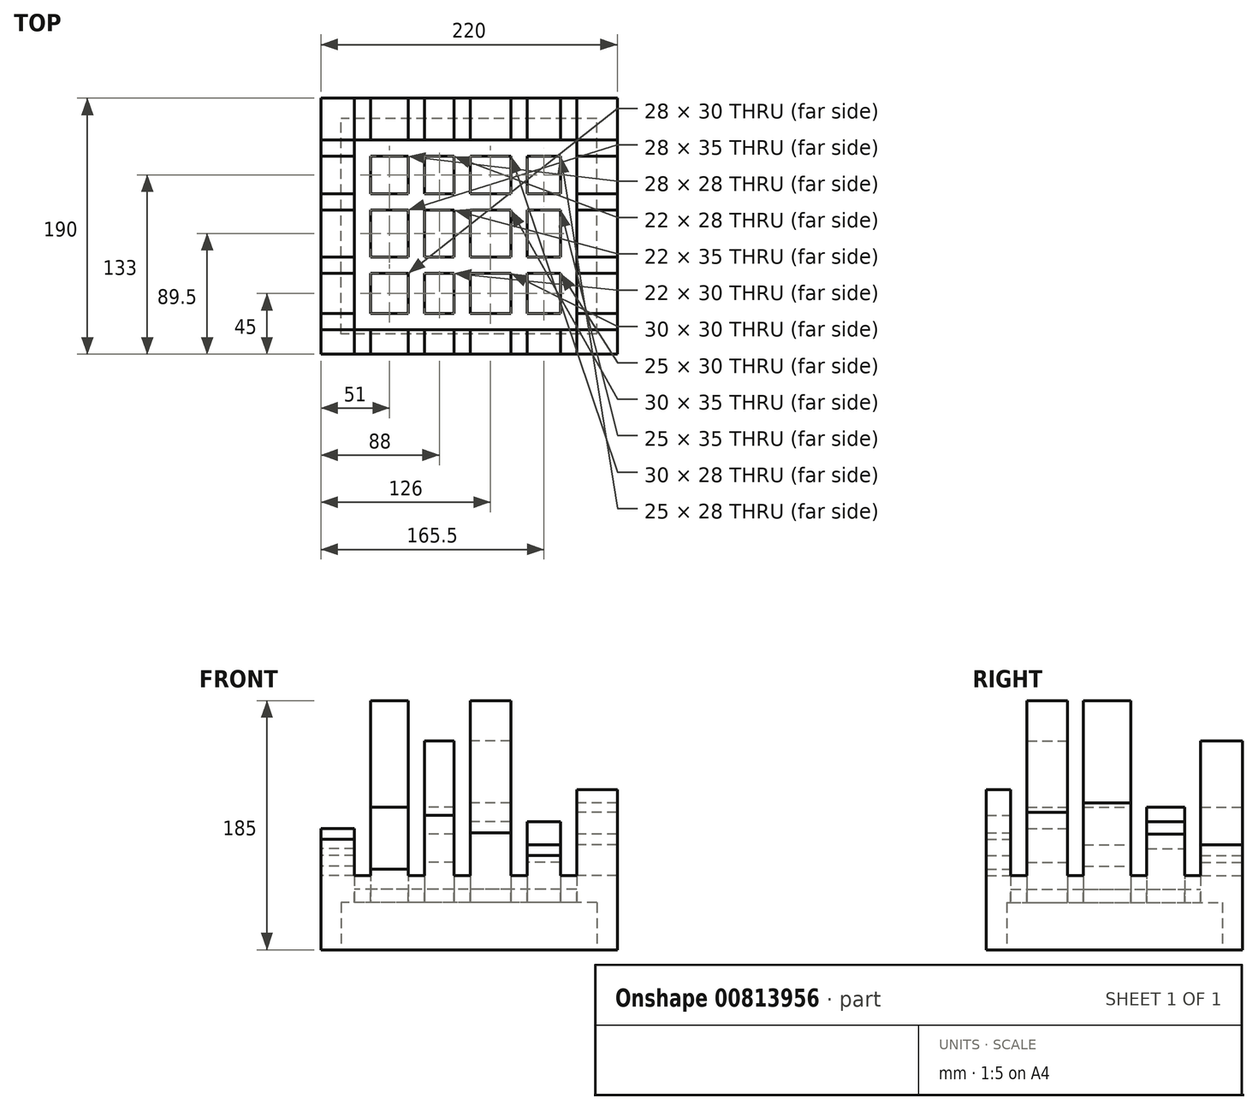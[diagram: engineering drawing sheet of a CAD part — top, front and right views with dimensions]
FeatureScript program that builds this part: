
annotation { "Feature Type Name" : "Feature", "Feature Type Description" : "" }
export const myFeature = defineFeature(function(context is Context, id is Id, definition is map)
    precondition{}
    {
        {
            var Q0;
            Q0=qCreatedBy(makeId("Top.planeOp"),FACE);
            var sketch = newSketch(context, id + "F0", { "sketchPlane" : qUnion([Q0])});
            skLineSegment(sketch, "E0.bottom", {"start": v(110, -95) * mm, "end": v(-110, -95) * mm});
            skLineSegment(sketch, "E0.top", {"start": v(110, 95) * mm, "end": v(-110, 95) * mm});
            skLineSegment(sketch, "E0.left", {"start": v(110, -95) * mm, "end": v(110, 95) * mm});
            skLineSegment(sketch, "E0.right", {"start": v(-110, -95) * mm, "end": v(-110, 95) * mm});
            skPoint(sketch, "E0.middle", {"position": v(0, 0) * mm});
            skLineSegment(sketch, "E1.0", {"start": v(-85, -95) * mm, "end": v(-85, 95) * mm});
            skLineSegment(sketch, "E2.0", {"start": v(-73, -95) * mm, "end": v(-73, 95) * mm});
            skLineSegment(sketch, "E3.0", {"start": v(-45, -95) * mm, "end": v(-45, 95) * mm});
            skLineSegment(sketch, "E4.0", {"start": v(-33, -95) * mm, "end": v(-33, 95) * mm});
            skLineSegment(sketch, "E5.0", {"start": v(-11, -95) * mm, "end": v(-11, 95) * mm});
            skLineSegment(sketch, "E6.0", {"start": v(1, -95) * mm, "end": v(1, 95) * mm});
            skLineSegment(sketch, "E7.0", {"start": v(31, -95) * mm, "end": v(31, 95) * mm});
            skLineSegment(sketch, "E8.0", {"start": v(43, -95) * mm, "end": v(43, 95) * mm});
            skLineSegment(sketch, "E9.0", {"start": v(68, -95) * mm, "end": v(68, 95) * mm});
            skLineSegment(sketch, "E10.0", {"start": v(80, -95) * mm, "end": v(80, 95) * mm});
            skLineSegment(sketch, "E11.0", {"start": v(110, -77) * mm, "end": v(-110, -77) * mm});
            skLineSegment(sketch, "E12.0", {"start": v(110, -65) * mm, "end": v(-110, -65) * mm});
            skLineSegment(sketch, "E13.0", {"start": v(110, -35) * mm, "end": v(-110, -35) * mm});
            skLineSegment(sketch, "E14.0", {"start": v(110, -23) * mm, "end": v(-110, -23) * mm});
            skLineSegment(sketch, "E15.0", {"start": v(110, 12) * mm, "end": v(-110, 12) * mm});
            skLineSegment(sketch, "E16.0", {"start": v(110, 24) * mm, "end": v(-110, 24) * mm});
            skLineSegment(sketch, "E17.0", {"start": v(110, 52) * mm, "end": v(-110, 52) * mm});
            skLineSegment(sketch, "E18.0", {"start": v(110, 64) * mm, "end": v(-110, 64) * mm});
            skSolve(sketch);
        }
        {
            var Q0;
            {var subQ0=sQuery(id+"F0.wireOp",EDGE,"E0.right");var subQ1=sQuery(id+"F0.wireOp",EDGE,"E0.top");var subQ2=makeQuery(id+"F0.imprint","INTERSECT",VERTEX,{"derivedFrom":[subQ1,subQ0]});Q0=makeQuery(id+"F0.imprint","IMPRINT",FACE,{"disambiguationData":[TD([[makeQuery(id+"F0.imprint","IMPRINT",EDGE,{"disambiguationData":[TD([[subQ2,1.0]])],"derivedFrom":subQ1}),1.0]])]});}
            extrude(context, id + "F1", {"entities" : qUnion([Q0]), "depth" : 25 * mm, "offsetDistance" : 25 * mm});
        }
        {
            var Q0;
            {var subQ0=sQuery(id+"F0.wireOp",EDGE,"E16.0");var subQ1=sQuery(id+"F0.wireOp",EDGE,"E0.right");var subQ2=makeQuery(id+"F0.imprint","INTERSECT",VERTEX,{"derivedFrom":[subQ1,subQ0]});Q0=makeQuery(id+"F0.imprint","IMPRINT",FACE,{"disambiguationData":[TD([[makeQuery(id+"F0.imprint","IMPRINT",EDGE,{"disambiguationData":[TD([[subQ2,-1.0]])],"derivedFrom":subQ1}),-1.0]])]});}
            extrude(context, id + "F2", {"entities" : qUnion([Q0]), "depth" : 30 * mm, "offsetDistance" : 25 * mm});
        }
        {
            var Q0;
            {var subQ0=sQuery(id+"F0.wireOp",EDGE,"E14.0");var subQ1=sQuery(id+"F0.wireOp",EDGE,"E0.right");var subQ2=makeQuery(id+"F0.imprint","INTERSECT",VERTEX,{"derivedFrom":[subQ1,subQ0]});Q0=makeQuery(id+"F0.imprint","IMPRINT",FACE,{"disambiguationData":[TD([[makeQuery(id+"F0.imprint","IMPRINT",EDGE,{"disambiguationData":[TD([[subQ2,-1.0]])],"derivedFrom":subQ1}),-1.0]])]});}
            extrude(context, id + "F3", {"entities" : qUnion([Q0]), "depth" : 17 * mm, "offsetDistance" : 25 * mm});
        }
        {
            var Q0;
            {var subQ0=sQuery(id+"F0.wireOp",EDGE,"E12.0");var subQ1=sQuery(id+"F0.wireOp",EDGE,"E0.right");var subQ2=makeQuery(id+"F0.imprint","INTERSECT",VERTEX,{"derivedFrom":[subQ1,subQ0]});Q0=makeQuery(id+"F0.imprint","IMPRINT",FACE,{"disambiguationData":[TD([[makeQuery(id+"F0.imprint","IMPRINT",EDGE,{"disambiguationData":[TD([[subQ2,-1.0]])],"derivedFrom":subQ1}),-1.0]])]});}
            extrude(context, id + "F4", {"entities" : qUnion([Q0]), "depth" : 45 * mm, "offsetDistance" : 25 * mm});
        }
        {
            var Q0;
            {var subQ0=sQuery(id+"F0.wireOp",EDGE,"E0.right");var subQ1=sQuery(id+"F0.wireOp",EDGE,"E0.bottom");var subQ2=makeQuery(id+"F0.imprint","INTERSECT",VERTEX,{"derivedFrom":[subQ1,subQ0]});Q0=makeQuery(id+"F0.imprint","IMPRINT",FACE,{"disambiguationData":[TD([[makeQuery(id+"F0.imprint","IMPRINT",EDGE,{"disambiguationData":[TD([[subQ2,1.0]])],"derivedFrom":subQ1}),-1.0]])]});}
            extrude(context, id + "F5", {"entities" : qUnion([Q0]), "depth" : 37 * mm, "offsetDistance" : 25 * mm});
        }
        {
            var Q0;
            {var subQ0=sQuery(id+"F0.wireOp",EDGE,"E2.0");var subQ1=sQuery(id+"F0.wireOp",EDGE,"E0.bottom");var subQ2=makeQuery(id+"F0.imprint","INTERSECT",VERTEX,{"derivedFrom":[subQ1,subQ0]});Q0=makeQuery(id+"F0.imprint","IMPRINT",FACE,{"disambiguationData":[TD([[makeQuery(id+"F0.imprint","IMPRINT",EDGE,{"disambiguationData":[TD([[subQ2,1.0]])],"derivedFrom":subQ1}),-1.0]])]});}
            extrude(context, id + "F6", {"entities" : qUnion([Q0]), "depth" : 15 * mm, "offsetDistance" : 25 * mm});
        }
        {
            var Q0;
            {var subQ0=sQuery(id+"F0.wireOp",EDGE,"E4.0");var subQ1=sQuery(id+"F0.wireOp",EDGE,"E0.bottom");var subQ2=makeQuery(id+"F0.imprint","INTERSECT",VERTEX,{"derivedFrom":[subQ1,subQ0]});Q0=makeQuery(id+"F0.imprint","IMPRINT",FACE,{"disambiguationData":[TD([[makeQuery(id+"F0.imprint","IMPRINT",EDGE,{"disambiguationData":[TD([[subQ2,1.0]])],"derivedFrom":subQ1}),-1.0]])]});}
            extrude(context, id + "F7", {"entities" : qUnion([Q0]), "depth" : 55 * mm, "offsetDistance" : 25 * mm});
        }
        {
            var Q0;
            {var subQ0=sQuery(id+"F0.wireOp",EDGE,"E6.0");var subQ1=sQuery(id+"F0.wireOp",EDGE,"E0.bottom");var subQ2=makeQuery(id+"F0.imprint","INTERSECT",VERTEX,{"derivedFrom":[subQ1,subQ0]});Q0=makeQuery(id+"F0.imprint","IMPRINT",FACE,{"disambiguationData":[TD([[makeQuery(id+"F0.imprint","IMPRINT",EDGE,{"disambiguationData":[TD([[subQ2,1.0]])],"derivedFrom":subQ1}),-1.0]])]});}
            extrude(context, id + "F8", {"entities" : qUnion([Q0]), "depth" : 42 * mm, "offsetDistance" : 25 * mm});
        }
        {
            var Q0;
            {var subQ0=sQuery(id+"F0.wireOp",EDGE,"E8.0");var subQ1=sQuery(id+"F0.wireOp",EDGE,"E0.bottom");var subQ2=makeQuery(id+"F0.imprint","INTERSECT",VERTEX,{"derivedFrom":[subQ1,subQ0]});Q0=makeQuery(id+"F0.imprint","IMPRINT",FACE,{"disambiguationData":[TD([[makeQuery(id+"F0.imprint","IMPRINT",EDGE,{"disambiguationData":[TD([[subQ2,1.0]])],"derivedFrom":subQ1}),-1.0]])]});}
            extrude(context, id + "F9", {"entities" : qUnion([Q0]), "depth" : 25 * mm, "offsetDistance" : 25 * mm});
        }
        {
            var Q0;
            {var subQ0=sQuery(id+"F0.wireOp",EDGE,"E0.left");var subQ1=sQuery(id+"F0.wireOp",EDGE,"E0.bottom");var subQ2=makeQuery(id+"F0.imprint","INTERSECT",VERTEX,{"derivedFrom":[subQ1,subQ0]});Q0=makeQuery(id+"F0.imprint","IMPRINT",FACE,{"disambiguationData":[TD([[makeQuery(id+"F0.imprint","IMPRINT",EDGE,{"disambiguationData":[TD([[subQ2,-1.0]])],"derivedFrom":subQ1}),-1.0]])]});}
            extrude(context, id + "F10", {"entities" : qUnion([Q0]), "depth" : 74 * mm, "offsetDistance" : 25 * mm});
        }
        {
            var Q0;
            {var subQ0=sQuery(id+"F0.wireOp",EDGE,"E12.0");var subQ1=sQuery(id+"F0.wireOp",EDGE,"E0.left");var subQ2=makeQuery(id+"F0.imprint","INTERSECT",VERTEX,{"derivedFrom":[subQ1,subQ0]});Q0=makeQuery(id+"F0.imprint","IMPRINT",FACE,{"disambiguationData":[TD([[makeQuery(id+"F0.imprint","IMPRINT",EDGE,{"disambiguationData":[TD([[subQ2,-1.0]])],"derivedFrom":subQ1}),1.0]])]});}
            extrude(context, id + "F11", {"entities" : qUnion([Q0]), "depth" : 57 * mm, "offsetDistance" : 25 * mm});
        }
        {
            var Q0;
            {var subQ0=sQuery(id+"F0.wireOp",EDGE,"E14.0");var subQ1=sQuery(id+"F0.wireOp",EDGE,"E0.left");var subQ2=makeQuery(id+"F0.imprint","INTERSECT",VERTEX,{"derivedFrom":[subQ1,subQ0]});Q0=makeQuery(id+"F0.imprint","IMPRINT",FACE,{"disambiguationData":[TD([[makeQuery(id+"F0.imprint","IMPRINT",EDGE,{"disambiguationData":[TD([[subQ2,-1.0]])],"derivedFrom":subQ1}),1.0]])]});}
            var Q1;
            {var subQ0=sQuery(id+"F0.wireOp",EDGE,"E14.0");var subQ1=sQuery(id+"F0.wireOp",EDGE,"E6.0");var subQ2=makeQuery(id+"F0.imprint","INTERSECT",VERTEX,{"derivedFrom":[subQ1,subQ0]});Q1=makeQuery(id+"F0.imprint","IMPRINT",FACE,{"disambiguationData":[TD([[makeQuery(id+"F0.imprint","IMPRINT",EDGE,{"disambiguationData":[TD([[subQ2,-1.0]])],"derivedFrom":subQ1}),-1.0]])]});}
            extrude(context, id + "F12", {"entities" : qUnion([Q0, Q1]), "depth" : 64 * mm, "offsetDistance" : 25 * mm});
        }
        {
            var Q0;
            {var subQ0=sQuery(id+"F0.wireOp",EDGE,"E16.0");var subQ1=sQuery(id+"F0.wireOp",EDGE,"E0.left");var subQ2=makeQuery(id+"F0.imprint","INTERSECT",VERTEX,{"derivedFrom":[subQ1,subQ0]});Q0=makeQuery(id+"F0.imprint","IMPRINT",FACE,{"disambiguationData":[TD([[makeQuery(id+"F0.imprint","IMPRINT",EDGE,{"disambiguationData":[TD([[subQ2,-1.0]])],"derivedFrom":subQ1}),1.0]])]});}
            var Q1;
            {var subQ0=sQuery(id+"F0.wireOp",EDGE,"E16.0");var subQ1=sQuery(id+"F0.wireOp",EDGE,"E4.0");var subQ2=makeQuery(id+"F0.imprint","INTERSECT",VERTEX,{"derivedFrom":[subQ1,subQ0]});Q1=makeQuery(id+"F0.imprint","IMPRINT",FACE,{"disambiguationData":[TD([[makeQuery(id+"F0.imprint","IMPRINT",EDGE,{"disambiguationData":[TD([[subQ2,-1.0]])],"derivedFrom":subQ1}),-1.0]])]});}
            extrude(context, id + "F13", {"entities" : qUnion([Q0, Q1]), "depth" : 41 * mm, "offsetDistance" : 25 * mm});
        }
        {
            var Q0;
            {var subQ0=sQuery(id+"F0.wireOp",EDGE,"E0.left");var subQ1=sQuery(id+"F0.wireOp",EDGE,"E0.top");var subQ2=makeQuery(id+"F0.imprint","INTERSECT",VERTEX,{"derivedFrom":[subQ1,subQ0]});Q0=makeQuery(id+"F0.imprint","IMPRINT",FACE,{"disambiguationData":[TD([[makeQuery(id+"F0.imprint","IMPRINT",EDGE,{"disambiguationData":[TD([[subQ2,-1.0]])],"derivedFrom":subQ1}),1.0]])]});}
            var Q1;
            {var subQ0=sQuery(id+"F0.wireOp",EDGE,"E14.0");var subQ1=sQuery(id+"F0.wireOp",EDGE,"E8.0");var subQ2=makeQuery(id+"F0.imprint","INTERSECT",VERTEX,{"derivedFrom":[subQ1,subQ0]});Q1=makeQuery(id+"F0.imprint","IMPRINT",FACE,{"disambiguationData":[TD([[makeQuery(id+"F0.imprint","IMPRINT",EDGE,{"disambiguationData":[TD([[subQ2,-1.0]])],"derivedFrom":subQ1}),-1.0]])]});}
            extrude(context, id + "F14", {"entities" : qUnion([Q0, Q1]), "depth" : 33 * mm, "offsetDistance" : 25 * mm});
        }
        {
            var Q0;
            {var subQ0=sQuery(id+"F0.wireOp",EDGE,"E6.0");var subQ1=sQuery(id+"F0.wireOp",EDGE,"E0.top");var subQ2=makeQuery(id+"F0.imprint","INTERSECT",VERTEX,{"derivedFrom":[subQ1,subQ0]});Q0=makeQuery(id+"F0.imprint","IMPRINT",FACE,{"disambiguationData":[TD([[makeQuery(id+"F0.imprint","IMPRINT",EDGE,{"disambiguationData":[TD([[subQ2,1.0]])],"derivedFrom":subQ1}),1.0]])]});}
            var Q1;
            {var subQ0=sQuery(id+"F0.wireOp",EDGE,"E12.0");var subQ1=sQuery(id+"F0.wireOp",EDGE,"E4.0");var subQ2=makeQuery(id+"F0.imprint","INTERSECT",VERTEX,{"derivedFrom":[subQ1,subQ0]});Q1=makeQuery(id+"F0.imprint","IMPRINT",FACE,{"disambiguationData":[TD([[makeQuery(id+"F0.imprint","IMPRINT",EDGE,{"disambiguationData":[TD([[subQ2,-1.0]])],"derivedFrom":subQ1}),-1.0]])]});}
            extrude(context, id + "F15", {"entities" : qUnion([Q0, Q1]), "depth" : 110 * mm, "offsetDistance" : 25 * mm});
        }
        {
            var Q0;
            {var subQ0=sQuery(id+"F0.wireOp",EDGE,"E14.0");var subQ1=sQuery(id+"F0.wireOp",EDGE,"E2.0");var subQ2=makeQuery(id+"F0.imprint","INTERSECT",VERTEX,{"derivedFrom":[subQ1,subQ0]});Q0=makeQuery(id+"F0.imprint","IMPRINT",FACE,{"disambiguationData":[TD([[makeQuery(id+"F0.imprint","IMPRINT",EDGE,{"disambiguationData":[TD([[subQ2,-1.0]])],"derivedFrom":subQ1}),-1.0]])]});}
            var Q1;
            {var subQ0=sQuery(id+"F0.wireOp",EDGE,"E12.0");var subQ1=sQuery(id+"F0.wireOp",EDGE,"E6.0");var subQ2=makeQuery(id+"F0.imprint","INTERSECT",VERTEX,{"derivedFrom":[subQ1,subQ0]});Q1=makeQuery(id+"F0.imprint","IMPRINT",FACE,{"disambiguationData":[TD([[makeQuery(id+"F0.imprint","IMPRINT",EDGE,{"disambiguationData":[TD([[subQ2,-1.0]])],"derivedFrom":subQ1}),-1.0]])]});}
            extrude(context, id + "F16", {"entities" : qUnion([Q0, Q1]), "depth" : 140 * mm, "offsetDistance" : 25 * mm});
        }
        {
            var Q0;
            {var subQ0=sQuery(id+"F0.wireOp",EDGE,"E16.0");var subQ1=sQuery(id+"F0.wireOp",EDGE,"E6.0");var subQ2=makeQuery(id+"F0.imprint","INTERSECT",VERTEX,{"derivedFrom":[subQ1,subQ0]});Q0=makeQuery(id+"F0.imprint","IMPRINT",FACE,{"disambiguationData":[TD([[makeQuery(id+"F0.imprint","IMPRINT",EDGE,{"disambiguationData":[TD([[subQ2,-1.0]])],"derivedFrom":subQ1}),-1.0]])]});}
            var Q1;
            {var subQ0=sQuery(id+"F0.wireOp",EDGE,"E16.0");var subQ1=sQuery(id+"F0.wireOp",EDGE,"E8.0");var subQ2=makeQuery(id+"F0.imprint","INTERSECT",VERTEX,{"derivedFrom":[subQ1,subQ0]});Q1=makeQuery(id+"F0.imprint","IMPRINT",FACE,{"disambiguationData":[TD([[makeQuery(id+"F0.imprint","IMPRINT",EDGE,{"disambiguationData":[TD([[subQ2,-1.0]])],"derivedFrom":subQ1}),-1.0]])]});}
            extrude(context, id + "F17", {"entities" : qUnion([Q0, Q1]), "depth" : 50 * mm, "offsetDistance" : 25 * mm});
        }
        {
            var Q0;
            {var subQ0=sQuery(id+"F0.wireOp",EDGE,"E2.0");var subQ1=sQuery(id+"F0.wireOp",EDGE,"E0.top");var subQ2=makeQuery(id+"F0.imprint","INTERSECT",VERTEX,{"derivedFrom":[subQ1,subQ0]});Q0=makeQuery(id+"F0.imprint","IMPRINT",FACE,{"disambiguationData":[TD([[makeQuery(id+"F0.imprint","IMPRINT",EDGE,{"disambiguationData":[TD([[subQ2,1.0]])],"derivedFrom":subQ1}),1.0]])]});}
            var Q1;
            {var subQ0=sQuery(id+"F0.wireOp",EDGE,"E16.0");var subQ1=sQuery(id+"F0.wireOp",EDGE,"E2.0");var subQ2=makeQuery(id+"F0.imprint","INTERSECT",VERTEX,{"derivedFrom":[subQ1,subQ0]});Q1=makeQuery(id+"F0.imprint","IMPRINT",FACE,{"disambiguationData":[TD([[makeQuery(id+"F0.imprint","IMPRINT",EDGE,{"disambiguationData":[TD([[subQ2,-1.0]])],"derivedFrom":subQ1}),-1.0]])]});}
            var Q2;
            {var subQ0=sQuery(id+"F0.wireOp",EDGE,"E14.0");var subQ1=sQuery(id+"F0.wireOp",EDGE,"E4.0");var subQ2=makeQuery(id+"F0.imprint","INTERSECT",VERTEX,{"derivedFrom":[subQ1,subQ0]});Q2=makeQuery(id+"F0.imprint","IMPRINT",FACE,{"disambiguationData":[TD([[makeQuery(id+"F0.imprint","IMPRINT",EDGE,{"disambiguationData":[TD([[subQ2,-1.0]])],"derivedFrom":subQ1}),-1.0]])]});}
            var Q3;
            {var subQ0=sQuery(id+"F0.wireOp",EDGE,"E12.0");var subQ1=sQuery(id+"F0.wireOp",EDGE,"E2.0");var subQ2=makeQuery(id+"F0.imprint","INTERSECT",VERTEX,{"derivedFrom":[subQ1,subQ0]});Q3=makeQuery(id+"F0.imprint","IMPRINT",FACE,{"disambiguationData":[TD([[makeQuery(id+"F0.imprint","IMPRINT",EDGE,{"disambiguationData":[TD([[subQ2,-1.0]])],"derivedFrom":subQ1}),-1.0]])]});}
            extrude(context, id + "F18", {"entities" : qUnion([Q0, Q1, Q2, Q3]), "depth" : 61 * mm, "offsetDistance" : 25 * mm});
        }
        {
            var Q0;
            {var subQ0=sQuery(id+"F0.wireOp",EDGE,"E4.0");var subQ1=sQuery(id+"F0.wireOp",EDGE,"E0.top");var subQ2=makeQuery(id+"F0.imprint","INTERSECT",VERTEX,{"derivedFrom":[subQ1,subQ0]});Q0=makeQuery(id+"F0.imprint","IMPRINT",FACE,{"disambiguationData":[TD([[makeQuery(id+"F0.imprint","IMPRINT",EDGE,{"disambiguationData":[TD([[subQ2,1.0]])],"derivedFrom":subQ1}),1.0]])]});}
            var Q1;
            {var subQ0=sQuery(id+"F0.wireOp",EDGE,"E8.0");var subQ1=sQuery(id+"F0.wireOp",EDGE,"E0.top");var subQ2=makeQuery(id+"F0.imprint","INTERSECT",VERTEX,{"derivedFrom":[subQ1,subQ0]});Q1=makeQuery(id+"F0.imprint","IMPRINT",FACE,{"disambiguationData":[TD([[makeQuery(id+"F0.imprint","IMPRINT",EDGE,{"disambiguationData":[TD([[subQ2,1.0]])],"derivedFrom":subQ1}),1.0]])]});}
            var Q2;
            {var subQ0=sQuery(id+"F0.wireOp",EDGE,"E12.0");var subQ1=sQuery(id+"F0.wireOp",EDGE,"E8.0");var subQ2=makeQuery(id+"F0.imprint","INTERSECT",VERTEX,{"derivedFrom":[subQ1,subQ0]});Q2=makeQuery(id+"F0.imprint","IMPRINT",FACE,{"disambiguationData":[TD([[makeQuery(id+"F0.imprint","IMPRINT",EDGE,{"disambiguationData":[TD([[subQ2,-1.0]])],"derivedFrom":subQ1}),-1.0]])]});}
            extrude(context, id + "F19", {"entities" : qUnion([Q0, Q1, Q2]), "depth" : 20 * mm, "offsetDistance" : 25 * mm});
        }
        {
            var Q0;
            {var subQ0=sQuery(id+"F0.wireOp",EDGE,"E17.0");var subQ1=sQuery(id+"F0.wireOp",EDGE,"E0.right");var subQ2=makeQuery(id+"F0.imprint","INTERSECT",VERTEX,{"derivedFrom":[subQ1,subQ0]});Q0=makeQuery(id+"F0.imprint","IMPRINT",FACE,{"disambiguationData":[TD([[makeQuery(id+"F0.imprint","IMPRINT",EDGE,{"disambiguationData":[TD([[subQ2,-1.0]])],"derivedFrom":subQ1}),-1.0]])]});}
            var Q1;
            {var subQ0=sQuery(id+"F0.wireOp",EDGE,"E15.0");var subQ1=sQuery(id+"F0.wireOp",EDGE,"E0.right");var subQ2=makeQuery(id+"F0.imprint","INTERSECT",VERTEX,{"derivedFrom":[subQ1,subQ0]});Q1=makeQuery(id+"F0.imprint","IMPRINT",FACE,{"disambiguationData":[TD([[makeQuery(id+"F0.imprint","IMPRINT",EDGE,{"disambiguationData":[TD([[subQ2,-1.0]])],"derivedFrom":subQ1}),-1.0]])]});}
            var Q2;
            {var subQ0=sQuery(id+"F0.wireOp",EDGE,"E13.0");var subQ1=sQuery(id+"F0.wireOp",EDGE,"E0.right");var subQ2=makeQuery(id+"F0.imprint","INTERSECT",VERTEX,{"derivedFrom":[subQ1,subQ0]});Q2=makeQuery(id+"F0.imprint","IMPRINT",FACE,{"disambiguationData":[TD([[makeQuery(id+"F0.imprint","IMPRINT",EDGE,{"disambiguationData":[TD([[subQ2,-1.0]])],"derivedFrom":subQ1}),-1.0]])]});}
            var Q3;
            {var subQ0=sQuery(id+"F0.wireOp",EDGE,"E11.0");var subQ1=sQuery(id+"F0.wireOp",EDGE,"E0.right");var subQ2=makeQuery(id+"F0.imprint","INTERSECT",VERTEX,{"derivedFrom":[subQ1,subQ0]});Q3=makeQuery(id+"F0.imprint","IMPRINT",FACE,{"disambiguationData":[TD([[makeQuery(id+"F0.imprint","IMPRINT",EDGE,{"disambiguationData":[TD([[subQ2,-1.0]])],"derivedFrom":subQ1}),-1.0]])]});}
            var Q4;
            {var subQ0=sQuery(id+"F0.wireOp",EDGE,"E1.0");var subQ1=sQuery(id+"F0.wireOp",EDGE,"E0.bottom");var subQ2=makeQuery(id+"F0.imprint","INTERSECT",VERTEX,{"derivedFrom":[subQ1,subQ0]});Q4=makeQuery(id+"F0.imprint","IMPRINT",FACE,{"disambiguationData":[TD([[makeQuery(id+"F0.imprint","IMPRINT",EDGE,{"disambiguationData":[TD([[subQ2,1.0]])],"derivedFrom":subQ1}),-1.0]])]});}
            var Q5;
            {var subQ0=sQuery(id+"F0.wireOp",EDGE,"E3.0");var subQ1=sQuery(id+"F0.wireOp",EDGE,"E0.bottom");var subQ2=makeQuery(id+"F0.imprint","INTERSECT",VERTEX,{"derivedFrom":[subQ1,subQ0]});Q5=makeQuery(id+"F0.imprint","IMPRINT",FACE,{"disambiguationData":[TD([[makeQuery(id+"F0.imprint","IMPRINT",EDGE,{"disambiguationData":[TD([[subQ2,1.0]])],"derivedFrom":subQ1}),-1.0]])]});}
            var Q6;
            {var subQ0=sQuery(id+"F0.wireOp",EDGE,"E5.0");var subQ1=sQuery(id+"F0.wireOp",EDGE,"E0.bottom");var subQ2=makeQuery(id+"F0.imprint","INTERSECT",VERTEX,{"derivedFrom":[subQ1,subQ0]});Q6=makeQuery(id+"F0.imprint","IMPRINT",FACE,{"disambiguationData":[TD([[makeQuery(id+"F0.imprint","IMPRINT",EDGE,{"disambiguationData":[TD([[subQ2,1.0]])],"derivedFrom":subQ1}),-1.0]])]});}
            var Q7;
            {var subQ0=sQuery(id+"F0.wireOp",EDGE,"E7.0");var subQ1=sQuery(id+"F0.wireOp",EDGE,"E0.bottom");var subQ2=makeQuery(id+"F0.imprint","INTERSECT",VERTEX,{"derivedFrom":[subQ1,subQ0]});Q7=makeQuery(id+"F0.imprint","IMPRINT",FACE,{"disambiguationData":[TD([[makeQuery(id+"F0.imprint","IMPRINT",EDGE,{"disambiguationData":[TD([[subQ2,1.0]])],"derivedFrom":subQ1}),-1.0]])]});}
            var Q8;
            {var subQ0=sQuery(id+"F0.wireOp",EDGE,"E9.0");var subQ1=sQuery(id+"F0.wireOp",EDGE,"E0.bottom");var subQ2=makeQuery(id+"F0.imprint","INTERSECT",VERTEX,{"derivedFrom":[subQ1,subQ0]});Q8=makeQuery(id+"F0.imprint","IMPRINT",FACE,{"disambiguationData":[TD([[makeQuery(id+"F0.imprint","IMPRINT",EDGE,{"disambiguationData":[TD([[subQ2,1.0]])],"derivedFrom":subQ1}),-1.0]])]});}
            var Q9;
            {var subQ0=sQuery(id+"F0.wireOp",EDGE,"E11.0");var subQ1=sQuery(id+"F0.wireOp",EDGE,"E0.left");var subQ2=makeQuery(id+"F0.imprint","INTERSECT",VERTEX,{"derivedFrom":[subQ1,subQ0]});Q9=makeQuery(id+"F0.imprint","IMPRINT",FACE,{"disambiguationData":[TD([[makeQuery(id+"F0.imprint","IMPRINT",EDGE,{"disambiguationData":[TD([[subQ2,-1.0]])],"derivedFrom":subQ1}),1.0]])]});}
            var Q10;
            {var subQ0=sQuery(id+"F0.wireOp",EDGE,"E13.0");var subQ1=sQuery(id+"F0.wireOp",EDGE,"E0.left");var subQ2=makeQuery(id+"F0.imprint","INTERSECT",VERTEX,{"derivedFrom":[subQ1,subQ0]});Q10=makeQuery(id+"F0.imprint","IMPRINT",FACE,{"disambiguationData":[TD([[makeQuery(id+"F0.imprint","IMPRINT",EDGE,{"disambiguationData":[TD([[subQ2,-1.0]])],"derivedFrom":subQ1}),1.0]])]});}
            var Q11;
            {var subQ0=sQuery(id+"F0.wireOp",EDGE,"E15.0");var subQ1=sQuery(id+"F0.wireOp",EDGE,"E0.left");var subQ2=makeQuery(id+"F0.imprint","INTERSECT",VERTEX,{"derivedFrom":[subQ1,subQ0]});Q11=makeQuery(id+"F0.imprint","IMPRINT",FACE,{"disambiguationData":[TD([[makeQuery(id+"F0.imprint","IMPRINT",EDGE,{"disambiguationData":[TD([[subQ2,-1.0]])],"derivedFrom":subQ1}),1.0]])]});}
            var Q12;
            {var subQ0=sQuery(id+"F0.wireOp",EDGE,"E17.0");var subQ1=sQuery(id+"F0.wireOp",EDGE,"E0.left");var subQ2=makeQuery(id+"F0.imprint","INTERSECT",VERTEX,{"derivedFrom":[subQ1,subQ0]});Q12=makeQuery(id+"F0.imprint","IMPRINT",FACE,{"disambiguationData":[TD([[makeQuery(id+"F0.imprint","IMPRINT",EDGE,{"disambiguationData":[TD([[subQ2,-1.0]])],"derivedFrom":subQ1}),1.0]])]});}
            var Q13;
            {var subQ0=sQuery(id+"F0.wireOp",EDGE,"E9.0");var subQ1=sQuery(id+"F0.wireOp",EDGE,"E0.top");var subQ2=makeQuery(id+"F0.imprint","INTERSECT",VERTEX,{"derivedFrom":[subQ1,subQ0]});Q13=makeQuery(id+"F0.imprint","IMPRINT",FACE,{"disambiguationData":[TD([[makeQuery(id+"F0.imprint","IMPRINT",EDGE,{"disambiguationData":[TD([[subQ2,1.0]])],"derivedFrom":subQ1}),1.0]])]});}
            var Q14;
            {var subQ0=sQuery(id+"F0.wireOp",EDGE,"E7.0");var subQ1=sQuery(id+"F0.wireOp",EDGE,"E0.top");var subQ2=makeQuery(id+"F0.imprint","INTERSECT",VERTEX,{"derivedFrom":[subQ1,subQ0]});Q14=makeQuery(id+"F0.imprint","IMPRINT",FACE,{"disambiguationData":[TD([[makeQuery(id+"F0.imprint","IMPRINT",EDGE,{"disambiguationData":[TD([[subQ2,1.0]])],"derivedFrom":subQ1}),1.0]])]});}
            var Q15;
            {var subQ0=sQuery(id+"F0.wireOp",EDGE,"E5.0");var subQ1=sQuery(id+"F0.wireOp",EDGE,"E0.top");var subQ2=makeQuery(id+"F0.imprint","INTERSECT",VERTEX,{"derivedFrom":[subQ1,subQ0]});Q15=makeQuery(id+"F0.imprint","IMPRINT",FACE,{"disambiguationData":[TD([[makeQuery(id+"F0.imprint","IMPRINT",EDGE,{"disambiguationData":[TD([[subQ2,1.0]])],"derivedFrom":subQ1}),1.0]])]});}
            var Q16;
            {var subQ0=sQuery(id+"F0.wireOp",EDGE,"E3.0");var subQ1=sQuery(id+"F0.wireOp",EDGE,"E0.top");var subQ2=makeQuery(id+"F0.imprint","INTERSECT",VERTEX,{"derivedFrom":[subQ1,subQ0]});Q16=makeQuery(id+"F0.imprint","IMPRINT",FACE,{"disambiguationData":[TD([[makeQuery(id+"F0.imprint","IMPRINT",EDGE,{"disambiguationData":[TD([[subQ2,1.0]])],"derivedFrom":subQ1}),1.0]])]});}
            var Q17;
            {var subQ0=sQuery(id+"F0.wireOp",EDGE,"E1.0");var subQ1=sQuery(id+"F0.wireOp",EDGE,"E0.top");var subQ2=makeQuery(id+"F0.imprint","INTERSECT",VERTEX,{"derivedFrom":[subQ1,subQ0]});Q17=makeQuery(id+"F0.imprint","IMPRINT",FACE,{"disambiguationData":[TD([[makeQuery(id+"F0.imprint","IMPRINT",EDGE,{"disambiguationData":[TD([[subQ2,1.0]])],"derivedFrom":subQ1}),1.0]])]});}
            extrude(context, id + "F20", {"entities" : qUnion([Q0, Q1, Q2, Q3, Q4, Q5, Q6, Q7, Q8, Q9, Q10, Q11, Q12, Q13, Q14, Q15, Q16, Q17]), "operationType" : NewBodyOperationType.ADD, "depth" : 10 * mm, "offsetDistance" : 25 * mm});
        }
        {
            var Q0;
            {var subQ0=sQuery(id+"F0.wireOp",EDGE,"E0.left");var subQ1=sQuery(id+"F0.wireOp",EDGE,"E0.bottom");var subQ2=makeQuery(id+"F0.imprint","INTERSECT",VERTEX,{"derivedFrom":[subQ1,subQ0]});Q0=makeQuery(id+"F0.imprint","IMPRINT",FACE,{"disambiguationData":[TD([[makeQuery(id+"F0.imprint","IMPRINT",EDGE,{"disambiguationData":[TD([[subQ2,-1.0]])],"derivedFrom":subQ1}),-1.0]])]});}
            var Q1;
            {var subQ0=sQuery(id+"F0.wireOp",EDGE,"E0.right");var subQ1=sQuery(id+"F0.wireOp",EDGE,"E0.bottom");var subQ2=makeQuery(id+"F0.imprint","INTERSECT",VERTEX,{"derivedFrom":[subQ1,subQ0]});Q1=makeQuery(id+"F0.imprint","IMPRINT",FACE,{"disambiguationData":[TD([[makeQuery(id+"F0.imprint","IMPRINT",EDGE,{"disambiguationData":[TD([[subQ2,1.0]])],"derivedFrom":subQ1}),-1.0]])]});}
            var Q2;
            {var subQ0=sQuery(id+"F0.wireOp",EDGE,"E0.left");var subQ1=sQuery(id+"F0.wireOp",EDGE,"E0.top");var subQ2=makeQuery(id+"F0.imprint","INTERSECT",VERTEX,{"derivedFrom":[subQ1,subQ0]});Q2=makeQuery(id+"F0.imprint","IMPRINT",FACE,{"disambiguationData":[TD([[makeQuery(id+"F0.imprint","IMPRINT",EDGE,{"disambiguationData":[TD([[subQ2,-1.0]])],"derivedFrom":subQ1}),1.0]])]});}
            var Q3;
            {var subQ0=sQuery(id+"F0.wireOp",EDGE,"E0.right");var subQ1=sQuery(id+"F0.wireOp",EDGE,"E0.top");var subQ2=makeQuery(id+"F0.imprint","INTERSECT",VERTEX,{"derivedFrom":[subQ1,subQ0]});Q3=makeQuery(id+"F0.imprint","IMPRINT",FACE,{"disambiguationData":[TD([[makeQuery(id+"F0.imprint","IMPRINT",EDGE,{"disambiguationData":[TD([[subQ2,1.0]])],"derivedFrom":subQ1}),1.0]])]});}
            var Q4;
            {var subQ0=sQuery(id+"F0.wireOp",EDGE,"E9.0");var subQ1=sQuery(id+"F0.wireOp",EDGE,"E0.bottom");var subQ2=makeQuery(id+"F0.imprint","INTERSECT",VERTEX,{"derivedFrom":[subQ1,subQ0]});Q4=makeQuery(id+"F0.imprint","IMPRINT",FACE,{"disambiguationData":[TD([[makeQuery(id+"F0.imprint","IMPRINT",EDGE,{"disambiguationData":[TD([[subQ2,1.0]])],"derivedFrom":subQ1}),-1.0]])]});}
            var Q5;
            {var subQ0=sQuery(id+"F0.wireOp",EDGE,"E8.0");var subQ1=sQuery(id+"F0.wireOp",EDGE,"E0.bottom");var subQ2=makeQuery(id+"F0.imprint","INTERSECT",VERTEX,{"derivedFrom":[subQ1,subQ0]});Q5=makeQuery(id+"F0.imprint","IMPRINT",FACE,{"disambiguationData":[TD([[makeQuery(id+"F0.imprint","IMPRINT",EDGE,{"disambiguationData":[TD([[subQ2,1.0]])],"derivedFrom":subQ1}),-1.0]])]});}
            var Q6;
            {var subQ0=sQuery(id+"F0.wireOp",EDGE,"E7.0");var subQ1=sQuery(id+"F0.wireOp",EDGE,"E0.bottom");var subQ2=makeQuery(id+"F0.imprint","INTERSECT",VERTEX,{"derivedFrom":[subQ1,subQ0]});Q6=makeQuery(id+"F0.imprint","IMPRINT",FACE,{"disambiguationData":[TD([[makeQuery(id+"F0.imprint","IMPRINT",EDGE,{"disambiguationData":[TD([[subQ2,1.0]])],"derivedFrom":subQ1}),-1.0]])]});}
            var Q7;
            {var subQ0=sQuery(id+"F0.wireOp",EDGE,"E6.0");var subQ1=sQuery(id+"F0.wireOp",EDGE,"E0.bottom");var subQ2=makeQuery(id+"F0.imprint","INTERSECT",VERTEX,{"derivedFrom":[subQ1,subQ0]});Q7=makeQuery(id+"F0.imprint","IMPRINT",FACE,{"disambiguationData":[TD([[makeQuery(id+"F0.imprint","IMPRINT",EDGE,{"disambiguationData":[TD([[subQ2,1.0]])],"derivedFrom":subQ1}),-1.0]])]});}
            var Q8;
            {var subQ0=sQuery(id+"F0.wireOp",EDGE,"E5.0");var subQ1=sQuery(id+"F0.wireOp",EDGE,"E0.bottom");var subQ2=makeQuery(id+"F0.imprint","INTERSECT",VERTEX,{"derivedFrom":[subQ1,subQ0]});Q8=makeQuery(id+"F0.imprint","IMPRINT",FACE,{"disambiguationData":[TD([[makeQuery(id+"F0.imprint","IMPRINT",EDGE,{"disambiguationData":[TD([[subQ2,1.0]])],"derivedFrom":subQ1}),-1.0]])]});}
            var Q9;
            {var subQ0=sQuery(id+"F0.wireOp",EDGE,"E4.0");var subQ1=sQuery(id+"F0.wireOp",EDGE,"E0.bottom");var subQ2=makeQuery(id+"F0.imprint","INTERSECT",VERTEX,{"derivedFrom":[subQ1,subQ0]});Q9=makeQuery(id+"F0.imprint","IMPRINT",FACE,{"disambiguationData":[TD([[makeQuery(id+"F0.imprint","IMPRINT",EDGE,{"disambiguationData":[TD([[subQ2,1.0]])],"derivedFrom":subQ1}),-1.0]])]});}
            var Q10;
            {var subQ0=sQuery(id+"F0.wireOp",EDGE,"E3.0");var subQ1=sQuery(id+"F0.wireOp",EDGE,"E0.bottom");var subQ2=makeQuery(id+"F0.imprint","INTERSECT",VERTEX,{"derivedFrom":[subQ1,subQ0]});Q10=makeQuery(id+"F0.imprint","IMPRINT",FACE,{"disambiguationData":[TD([[makeQuery(id+"F0.imprint","IMPRINT",EDGE,{"disambiguationData":[TD([[subQ2,1.0]])],"derivedFrom":subQ1}),-1.0]])]});}
            var Q11;
            {var subQ0=sQuery(id+"F0.wireOp",EDGE,"E2.0");var subQ1=sQuery(id+"F0.wireOp",EDGE,"E0.bottom");var subQ2=makeQuery(id+"F0.imprint","INTERSECT",VERTEX,{"derivedFrom":[subQ1,subQ0]});Q11=makeQuery(id+"F0.imprint","IMPRINT",FACE,{"disambiguationData":[TD([[makeQuery(id+"F0.imprint","IMPRINT",EDGE,{"disambiguationData":[TD([[subQ2,1.0]])],"derivedFrom":subQ1}),-1.0]])]});}
            var Q12;
            {var subQ0=sQuery(id+"F0.wireOp",EDGE,"E1.0");var subQ1=sQuery(id+"F0.wireOp",EDGE,"E0.bottom");var subQ2=makeQuery(id+"F0.imprint","INTERSECT",VERTEX,{"derivedFrom":[subQ1,subQ0]});Q12=makeQuery(id+"F0.imprint","IMPRINT",FACE,{"disambiguationData":[TD([[makeQuery(id+"F0.imprint","IMPRINT",EDGE,{"disambiguationData":[TD([[subQ2,1.0]])],"derivedFrom":subQ1}),-1.0]])]});}
            var Q13;
            {var subQ0=sQuery(id+"F0.wireOp",EDGE,"E9.0");var subQ1=sQuery(id+"F0.wireOp",EDGE,"E0.top");var subQ2=makeQuery(id+"F0.imprint","INTERSECT",VERTEX,{"derivedFrom":[subQ1,subQ0]});Q13=makeQuery(id+"F0.imprint","IMPRINT",FACE,{"disambiguationData":[TD([[makeQuery(id+"F0.imprint","IMPRINT",EDGE,{"disambiguationData":[TD([[subQ2,1.0]])],"derivedFrom":subQ1}),1.0]])]});}
            var Q14;
            {var subQ0=sQuery(id+"F0.wireOp",EDGE,"E8.0");var subQ1=sQuery(id+"F0.wireOp",EDGE,"E0.top");var subQ2=makeQuery(id+"F0.imprint","INTERSECT",VERTEX,{"derivedFrom":[subQ1,subQ0]});Q14=makeQuery(id+"F0.imprint","IMPRINT",FACE,{"disambiguationData":[TD([[makeQuery(id+"F0.imprint","IMPRINT",EDGE,{"disambiguationData":[TD([[subQ2,1.0]])],"derivedFrom":subQ1}),1.0]])]});}
            var Q15;
            {var subQ0=sQuery(id+"F0.wireOp",EDGE,"E7.0");var subQ1=sQuery(id+"F0.wireOp",EDGE,"E0.top");var subQ2=makeQuery(id+"F0.imprint","INTERSECT",VERTEX,{"derivedFrom":[subQ1,subQ0]});Q15=makeQuery(id+"F0.imprint","IMPRINT",FACE,{"disambiguationData":[TD([[makeQuery(id+"F0.imprint","IMPRINT",EDGE,{"disambiguationData":[TD([[subQ2,1.0]])],"derivedFrom":subQ1}),1.0]])]});}
            var Q16;
            {var subQ0=sQuery(id+"F0.wireOp",EDGE,"E6.0");var subQ1=sQuery(id+"F0.wireOp",EDGE,"E0.top");var subQ2=makeQuery(id+"F0.imprint","INTERSECT",VERTEX,{"derivedFrom":[subQ1,subQ0]});Q16=makeQuery(id+"F0.imprint","IMPRINT",FACE,{"disambiguationData":[TD([[makeQuery(id+"F0.imprint","IMPRINT",EDGE,{"disambiguationData":[TD([[subQ2,1.0]])],"derivedFrom":subQ1}),1.0]])]});}
            var Q17;
            {var subQ0=sQuery(id+"F0.wireOp",EDGE,"E5.0");var subQ1=sQuery(id+"F0.wireOp",EDGE,"E0.top");var subQ2=makeQuery(id+"F0.imprint","INTERSECT",VERTEX,{"derivedFrom":[subQ1,subQ0]});Q17=makeQuery(id+"F0.imprint","IMPRINT",FACE,{"disambiguationData":[TD([[makeQuery(id+"F0.imprint","IMPRINT",EDGE,{"disambiguationData":[TD([[subQ2,1.0]])],"derivedFrom":subQ1}),1.0]])]});}
            var Q18;
            {var subQ0=sQuery(id+"F0.wireOp",EDGE,"E4.0");var subQ1=sQuery(id+"F0.wireOp",EDGE,"E0.top");var subQ2=makeQuery(id+"F0.imprint","INTERSECT",VERTEX,{"derivedFrom":[subQ1,subQ0]});Q18=makeQuery(id+"F0.imprint","IMPRINT",FACE,{"disambiguationData":[TD([[makeQuery(id+"F0.imprint","IMPRINT",EDGE,{"disambiguationData":[TD([[subQ2,1.0]])],"derivedFrom":subQ1}),1.0]])]});}
            var Q19;
            {var subQ0=sQuery(id+"F0.wireOp",EDGE,"E3.0");var subQ1=sQuery(id+"F0.wireOp",EDGE,"E0.top");var subQ2=makeQuery(id+"F0.imprint","INTERSECT",VERTEX,{"derivedFrom":[subQ1,subQ0]});Q19=makeQuery(id+"F0.imprint","IMPRINT",FACE,{"disambiguationData":[TD([[makeQuery(id+"F0.imprint","IMPRINT",EDGE,{"disambiguationData":[TD([[subQ2,1.0]])],"derivedFrom":subQ1}),1.0]])]});}
            var Q20;
            {var subQ0=sQuery(id+"F0.wireOp",EDGE,"E2.0");var subQ1=sQuery(id+"F0.wireOp",EDGE,"E0.top");var subQ2=makeQuery(id+"F0.imprint","INTERSECT",VERTEX,{"derivedFrom":[subQ1,subQ0]});Q20=makeQuery(id+"F0.imprint","IMPRINT",FACE,{"disambiguationData":[TD([[makeQuery(id+"F0.imprint","IMPRINT",EDGE,{"disambiguationData":[TD([[subQ2,1.0]])],"derivedFrom":subQ1}),1.0]])]});}
            var Q21;
            {var subQ0=sQuery(id+"F0.wireOp",EDGE,"E1.0");var subQ1=sQuery(id+"F0.wireOp",EDGE,"E0.top");var subQ2=makeQuery(id+"F0.imprint","INTERSECT",VERTEX,{"derivedFrom":[subQ1,subQ0]});Q21=makeQuery(id+"F0.imprint","IMPRINT",FACE,{"disambiguationData":[TD([[makeQuery(id+"F0.imprint","IMPRINT",EDGE,{"disambiguationData":[TD([[subQ2,1.0]])],"derivedFrom":subQ1}),1.0]])]});}
            var Q22;
            {var subQ0=sQuery(id+"F0.wireOp",EDGE,"E11.0");var subQ1=sQuery(id+"F0.wireOp",EDGE,"E0.left");var subQ2=makeQuery(id+"F0.imprint","INTERSECT",VERTEX,{"derivedFrom":[subQ1,subQ0]});Q22=makeQuery(id+"F0.imprint","IMPRINT",FACE,{"disambiguationData":[TD([[makeQuery(id+"F0.imprint","IMPRINT",EDGE,{"disambiguationData":[TD([[subQ2,-1.0]])],"derivedFrom":subQ1}),1.0]])]});}
            var Q23;
            {var subQ0=sQuery(id+"F0.wireOp",EDGE,"E12.0");var subQ1=sQuery(id+"F0.wireOp",EDGE,"E0.left");var subQ2=makeQuery(id+"F0.imprint","INTERSECT",VERTEX,{"derivedFrom":[subQ1,subQ0]});Q23=makeQuery(id+"F0.imprint","IMPRINT",FACE,{"disambiguationData":[TD([[makeQuery(id+"F0.imprint","IMPRINT",EDGE,{"disambiguationData":[TD([[subQ2,-1.0]])],"derivedFrom":subQ1}),1.0]])]});}
            var Q24;
            {var subQ0=sQuery(id+"F0.wireOp",EDGE,"E13.0");var subQ1=sQuery(id+"F0.wireOp",EDGE,"E0.left");var subQ2=makeQuery(id+"F0.imprint","INTERSECT",VERTEX,{"derivedFrom":[subQ1,subQ0]});Q24=makeQuery(id+"F0.imprint","IMPRINT",FACE,{"disambiguationData":[TD([[makeQuery(id+"F0.imprint","IMPRINT",EDGE,{"disambiguationData":[TD([[subQ2,-1.0]])],"derivedFrom":subQ1}),1.0]])]});}
            var Q25;
            {var subQ0=sQuery(id+"F0.wireOp",EDGE,"E14.0");var subQ1=sQuery(id+"F0.wireOp",EDGE,"E0.left");var subQ2=makeQuery(id+"F0.imprint","INTERSECT",VERTEX,{"derivedFrom":[subQ1,subQ0]});Q25=makeQuery(id+"F0.imprint","IMPRINT",FACE,{"disambiguationData":[TD([[makeQuery(id+"F0.imprint","IMPRINT",EDGE,{"disambiguationData":[TD([[subQ2,-1.0]])],"derivedFrom":subQ1}),1.0]])]});}
            var Q26;
            {var subQ0=sQuery(id+"F0.wireOp",EDGE,"E15.0");var subQ1=sQuery(id+"F0.wireOp",EDGE,"E0.left");var subQ2=makeQuery(id+"F0.imprint","INTERSECT",VERTEX,{"derivedFrom":[subQ1,subQ0]});Q26=makeQuery(id+"F0.imprint","IMPRINT",FACE,{"disambiguationData":[TD([[makeQuery(id+"F0.imprint","IMPRINT",EDGE,{"disambiguationData":[TD([[subQ2,-1.0]])],"derivedFrom":subQ1}),1.0]])]});}
            var Q27;
            {var subQ0=sQuery(id+"F0.wireOp",EDGE,"E16.0");var subQ1=sQuery(id+"F0.wireOp",EDGE,"E0.left");var subQ2=makeQuery(id+"F0.imprint","INTERSECT",VERTEX,{"derivedFrom":[subQ1,subQ0]});Q27=makeQuery(id+"F0.imprint","IMPRINT",FACE,{"disambiguationData":[TD([[makeQuery(id+"F0.imprint","IMPRINT",EDGE,{"disambiguationData":[TD([[subQ2,-1.0]])],"derivedFrom":subQ1}),1.0]])]});}
            var Q28;
            {var subQ0=sQuery(id+"F0.wireOp",EDGE,"E17.0");var subQ1=sQuery(id+"F0.wireOp",EDGE,"E0.left");var subQ2=makeQuery(id+"F0.imprint","INTERSECT",VERTEX,{"derivedFrom":[subQ1,subQ0]});Q28=makeQuery(id+"F0.imprint","IMPRINT",FACE,{"disambiguationData":[TD([[makeQuery(id+"F0.imprint","IMPRINT",EDGE,{"disambiguationData":[TD([[subQ2,-1.0]])],"derivedFrom":subQ1}),1.0]])]});}
            var Q29;
            {var subQ0=sQuery(id+"F0.wireOp",EDGE,"E11.0");var subQ1=sQuery(id+"F0.wireOp",EDGE,"E0.right");var subQ2=makeQuery(id+"F0.imprint","INTERSECT",VERTEX,{"derivedFrom":[subQ1,subQ0]});Q29=makeQuery(id+"F0.imprint","IMPRINT",FACE,{"disambiguationData":[TD([[makeQuery(id+"F0.imprint","IMPRINT",EDGE,{"disambiguationData":[TD([[subQ2,-1.0]])],"derivedFrom":subQ1}),-1.0]])]});}
            var Q30;
            {var subQ0=sQuery(id+"F0.wireOp",EDGE,"E12.0");var subQ1=sQuery(id+"F0.wireOp",EDGE,"E0.right");var subQ2=makeQuery(id+"F0.imprint","INTERSECT",VERTEX,{"derivedFrom":[subQ1,subQ0]});Q30=makeQuery(id+"F0.imprint","IMPRINT",FACE,{"disambiguationData":[TD([[makeQuery(id+"F0.imprint","IMPRINT",EDGE,{"disambiguationData":[TD([[subQ2,-1.0]])],"derivedFrom":subQ1}),-1.0]])]});}
            var Q31;
            {var subQ0=sQuery(id+"F0.wireOp",EDGE,"E13.0");var subQ1=sQuery(id+"F0.wireOp",EDGE,"E0.right");var subQ2=makeQuery(id+"F0.imprint","INTERSECT",VERTEX,{"derivedFrom":[subQ1,subQ0]});Q31=makeQuery(id+"F0.imprint","IMPRINT",FACE,{"disambiguationData":[TD([[makeQuery(id+"F0.imprint","IMPRINT",EDGE,{"disambiguationData":[TD([[subQ2,-1.0]])],"derivedFrom":subQ1}),-1.0]])]});}
            var Q32;
            {var subQ0=sQuery(id+"F0.wireOp",EDGE,"E14.0");var subQ1=sQuery(id+"F0.wireOp",EDGE,"E0.right");var subQ2=makeQuery(id+"F0.imprint","INTERSECT",VERTEX,{"derivedFrom":[subQ1,subQ0]});Q32=makeQuery(id+"F0.imprint","IMPRINT",FACE,{"disambiguationData":[TD([[makeQuery(id+"F0.imprint","IMPRINT",EDGE,{"disambiguationData":[TD([[subQ2,-1.0]])],"derivedFrom":subQ1}),-1.0]])]});}
            var Q33;
            {var subQ0=sQuery(id+"F0.wireOp",EDGE,"E15.0");var subQ1=sQuery(id+"F0.wireOp",EDGE,"E0.right");var subQ2=makeQuery(id+"F0.imprint","INTERSECT",VERTEX,{"derivedFrom":[subQ1,subQ0]});Q33=makeQuery(id+"F0.imprint","IMPRINT",FACE,{"disambiguationData":[TD([[makeQuery(id+"F0.imprint","IMPRINT",EDGE,{"disambiguationData":[TD([[subQ2,-1.0]])],"derivedFrom":subQ1}),-1.0]])]});}
            var Q34;
            {var subQ0=sQuery(id+"F0.wireOp",EDGE,"E16.0");var subQ1=sQuery(id+"F0.wireOp",EDGE,"E0.right");var subQ2=makeQuery(id+"F0.imprint","INTERSECT",VERTEX,{"derivedFrom":[subQ1,subQ0]});Q34=makeQuery(id+"F0.imprint","IMPRINT",FACE,{"disambiguationData":[TD([[makeQuery(id+"F0.imprint","IMPRINT",EDGE,{"disambiguationData":[TD([[subQ2,-1.0]])],"derivedFrom":subQ1}),-1.0]])]});}
            var Q35;
            {var subQ0=sQuery(id+"F0.wireOp",EDGE,"E17.0");var subQ1=sQuery(id+"F0.wireOp",EDGE,"E0.right");var subQ2=makeQuery(id+"F0.imprint","INTERSECT",VERTEX,{"derivedFrom":[subQ1,subQ0]});Q35=makeQuery(id+"F0.imprint","IMPRINT",FACE,{"disambiguationData":[TD([[makeQuery(id+"F0.imprint","IMPRINT",EDGE,{"disambiguationData":[TD([[subQ2,-1.0]])],"derivedFrom":subQ1}),-1.0]])]});}
            var Q36;
            {var subQ0=sQuery(id+"F0.wireOp",EDGE,"E12.0");var subQ1=sQuery(id+"F0.wireOp",EDGE,"E8.0");var subQ2=makeQuery(id+"F0.imprint","INTERSECT",VERTEX,{"derivedFrom":[subQ1,subQ0]});Q36=makeQuery(id+"F0.imprint","IMPRINT",FACE,{"disambiguationData":[TD([[makeQuery(id+"F0.imprint","IMPRINT",EDGE,{"disambiguationData":[TD([[subQ2,-1.0]])],"derivedFrom":subQ1}),-1.0]])]});}
            var Q37;
            {var subQ0=sQuery(id+"F0.wireOp",EDGE,"E12.0");var subQ1=sQuery(id+"F0.wireOp",EDGE,"E6.0");var subQ2=makeQuery(id+"F0.imprint","INTERSECT",VERTEX,{"derivedFrom":[subQ1,subQ0]});Q37=makeQuery(id+"F0.imprint","IMPRINT",FACE,{"disambiguationData":[TD([[makeQuery(id+"F0.imprint","IMPRINT",EDGE,{"disambiguationData":[TD([[subQ2,-1.0]])],"derivedFrom":subQ1}),-1.0]])]});}
            var Q38;
            {var subQ0=sQuery(id+"F0.wireOp",EDGE,"E12.0");var subQ1=sQuery(id+"F0.wireOp",EDGE,"E4.0");var subQ2=makeQuery(id+"F0.imprint","INTERSECT",VERTEX,{"derivedFrom":[subQ1,subQ0]});Q38=makeQuery(id+"F0.imprint","IMPRINT",FACE,{"disambiguationData":[TD([[makeQuery(id+"F0.imprint","IMPRINT",EDGE,{"disambiguationData":[TD([[subQ2,-1.0]])],"derivedFrom":subQ1}),-1.0]])]});}
            var Q39;
            {var subQ0=sQuery(id+"F0.wireOp",EDGE,"E17.0");var subQ1=sQuery(id+"F0.wireOp",EDGE,"E1.0");var subQ2=makeQuery(id+"F0.imprint","INTERSECT",VERTEX,{"derivedFrom":[subQ1,subQ0]});Q39=makeQuery(id+"F0.imprint","IMPRINT",FACE,{"disambiguationData":[TD([[makeQuery(id+"F0.imprint","IMPRINT",EDGE,{"disambiguationData":[TD([[subQ2,-1.0]])],"derivedFrom":subQ1}),-1.0]])]});}
            var Q40;
            {var subQ0=sQuery(id+"F0.wireOp",EDGE,"E16.0");var subQ1=sQuery(id+"F0.wireOp",EDGE,"E8.0");var subQ2=makeQuery(id+"F0.imprint","INTERSECT",VERTEX,{"derivedFrom":[subQ1,subQ0]});Q40=makeQuery(id+"F0.imprint","IMPRINT",FACE,{"disambiguationData":[TD([[makeQuery(id+"F0.imprint","IMPRINT",EDGE,{"disambiguationData":[TD([[subQ2,-1.0]])],"derivedFrom":subQ1}),-1.0]])]});}
            var Q41;
            {var subQ0=sQuery(id+"F0.wireOp",EDGE,"E14.0");var subQ1=sQuery(id+"F0.wireOp",EDGE,"E6.0");var subQ2=makeQuery(id+"F0.imprint","INTERSECT",VERTEX,{"derivedFrom":[subQ1,subQ0]});Q41=makeQuery(id+"F0.imprint","IMPRINT",FACE,{"disambiguationData":[TD([[makeQuery(id+"F0.imprint","IMPRINT",EDGE,{"disambiguationData":[TD([[subQ2,-1.0]])],"derivedFrom":subQ1}),-1.0]])]});}
            var Q42;
            {var subQ0=sQuery(id+"F0.wireOp",EDGE,"E17.0");var subQ1=sQuery(id+"F0.wireOp",EDGE,"E6.0");var subQ2=makeQuery(id+"F0.imprint","INTERSECT",VERTEX,{"derivedFrom":[subQ1,subQ0]});Q42=makeQuery(id+"F0.imprint","IMPRINT",FACE,{"disambiguationData":[TD([[makeQuery(id+"F0.imprint","IMPRINT",EDGE,{"disambiguationData":[TD([[subQ2,-1.0]])],"derivedFrom":subQ1}),-1.0]])]});}
            var Q43;
            {var subQ0=sQuery(id+"F0.wireOp",EDGE,"E13.0");var subQ1=sQuery(id+"F0.wireOp",EDGE,"E2.0");var subQ2=makeQuery(id+"F0.imprint","INTERSECT",VERTEX,{"derivedFrom":[subQ1,subQ0]});Q43=makeQuery(id+"F0.imprint","IMPRINT",FACE,{"disambiguationData":[TD([[makeQuery(id+"F0.imprint","IMPRINT",EDGE,{"disambiguationData":[TD([[subQ2,-1.0]])],"derivedFrom":subQ1}),-1.0]])]});}
            var Q44;
            {var subQ0=sQuery(id+"F0.wireOp",EDGE,"E12.0");var subQ1=sQuery(id+"F0.wireOp",EDGE,"E9.0");var subQ2=makeQuery(id+"F0.imprint","INTERSECT",VERTEX,{"derivedFrom":[subQ1,subQ0]});Q44=makeQuery(id+"F0.imprint","IMPRINT",FACE,{"disambiguationData":[TD([[makeQuery(id+"F0.imprint","IMPRINT",EDGE,{"disambiguationData":[TD([[subQ2,-1.0]])],"derivedFrom":subQ1}),-1.0]])]});}
            var Q45;
            {var subQ0=sQuery(id+"F0.wireOp",EDGE,"E13.0");var subQ1=sQuery(id+"F0.wireOp",EDGE,"E4.0");var subQ2=makeQuery(id+"F0.imprint","INTERSECT",VERTEX,{"derivedFrom":[subQ1,subQ0]});Q45=makeQuery(id+"F0.imprint","IMPRINT",FACE,{"disambiguationData":[TD([[makeQuery(id+"F0.imprint","IMPRINT",EDGE,{"disambiguationData":[TD([[subQ2,-1.0]])],"derivedFrom":subQ1}),-1.0]])]});}
            var Q46;
            {var subQ0=sQuery(id+"F0.wireOp",EDGE,"E11.0");var subQ1=sQuery(id+"F0.wireOp",EDGE,"E2.0");var subQ2=makeQuery(id+"F0.imprint","INTERSECT",VERTEX,{"derivedFrom":[subQ1,subQ0]});Q46=makeQuery(id+"F0.imprint","IMPRINT",FACE,{"disambiguationData":[TD([[makeQuery(id+"F0.imprint","IMPRINT",EDGE,{"disambiguationData":[TD([[subQ2,-1.0]])],"derivedFrom":subQ1}),-1.0]])]});}
            var Q47;
            {var subQ0=sQuery(id+"F0.wireOp",EDGE,"E17.0");var subQ1=sQuery(id+"F0.wireOp",EDGE,"E8.0");var subQ2=makeQuery(id+"F0.imprint","INTERSECT",VERTEX,{"derivedFrom":[subQ1,subQ0]});Q47=makeQuery(id+"F0.imprint","IMPRINT",FACE,{"disambiguationData":[TD([[makeQuery(id+"F0.imprint","IMPRINT",EDGE,{"disambiguationData":[TD([[subQ2,-1.0]])],"derivedFrom":subQ1}),-1.0]])]});}
            var Q48;
            {var subQ0=sQuery(id+"F0.wireOp",EDGE,"E11.0");var subQ1=sQuery(id+"F0.wireOp",EDGE,"E7.0");var subQ2=makeQuery(id+"F0.imprint","INTERSECT",VERTEX,{"derivedFrom":[subQ1,subQ0]});Q48=makeQuery(id+"F0.imprint","IMPRINT",FACE,{"disambiguationData":[TD([[makeQuery(id+"F0.imprint","IMPRINT",EDGE,{"disambiguationData":[TD([[subQ2,-1.0]])],"derivedFrom":subQ1}),-1.0]])]});}
            var Q49;
            {var subQ0=sQuery(id+"F0.wireOp",EDGE,"E16.0");var subQ1=sQuery(id+"F0.wireOp",EDGE,"E4.0");var subQ2=makeQuery(id+"F0.imprint","INTERSECT",VERTEX,{"derivedFrom":[subQ1,subQ0]});Q49=makeQuery(id+"F0.imprint","IMPRINT",FACE,{"disambiguationData":[TD([[makeQuery(id+"F0.imprint","IMPRINT",EDGE,{"disambiguationData":[TD([[subQ2,-1.0]])],"derivedFrom":subQ1}),-1.0]])]});}
            var Q50;
            {var subQ0=sQuery(id+"F0.wireOp",EDGE,"E14.0");var subQ1=sQuery(id+"F0.wireOp",EDGE,"E2.0");var subQ2=makeQuery(id+"F0.imprint","INTERSECT",VERTEX,{"derivedFrom":[subQ1,subQ0]});Q50=makeQuery(id+"F0.imprint","IMPRINT",FACE,{"disambiguationData":[TD([[makeQuery(id+"F0.imprint","IMPRINT",EDGE,{"disambiguationData":[TD([[subQ2,-1.0]])],"derivedFrom":subQ1}),-1.0]])]});}
            var Q51;
            {var subQ0=sQuery(id+"F0.wireOp",EDGE,"E13.0");var subQ1=sQuery(id+"F0.wireOp",EDGE,"E9.0");var subQ2=makeQuery(id+"F0.imprint","INTERSECT",VERTEX,{"derivedFrom":[subQ1,subQ0]});Q51=makeQuery(id+"F0.imprint","IMPRINT",FACE,{"disambiguationData":[TD([[makeQuery(id+"F0.imprint","IMPRINT",EDGE,{"disambiguationData":[TD([[subQ2,-1.0]])],"derivedFrom":subQ1}),-1.0]])]});}
            var Q52;
            {var subQ0=sQuery(id+"F0.wireOp",EDGE,"E14.0");var subQ1=sQuery(id+"F0.wireOp",EDGE,"E4.0");var subQ2=makeQuery(id+"F0.imprint","INTERSECT",VERTEX,{"derivedFrom":[subQ1,subQ0]});Q52=makeQuery(id+"F0.imprint","IMPRINT",FACE,{"disambiguationData":[TD([[makeQuery(id+"F0.imprint","IMPRINT",EDGE,{"disambiguationData":[TD([[subQ2,-1.0]])],"derivedFrom":subQ1}),-1.0]])]});}
            var Q53;
            {var subQ0=sQuery(id+"F0.wireOp",EDGE,"E12.0");var subQ1=sQuery(id+"F0.wireOp",EDGE,"E2.0");var subQ2=makeQuery(id+"F0.imprint","INTERSECT",VERTEX,{"derivedFrom":[subQ1,subQ0]});Q53=makeQuery(id+"F0.imprint","IMPRINT",FACE,{"disambiguationData":[TD([[makeQuery(id+"F0.imprint","IMPRINT",EDGE,{"disambiguationData":[TD([[subQ2,-1.0]])],"derivedFrom":subQ1}),-1.0]])]});}
            var Q54;
            {var subQ0=sQuery(id+"F0.wireOp",EDGE,"E11.0");var subQ1=sQuery(id+"F0.wireOp",EDGE,"E9.0");var subQ2=makeQuery(id+"F0.imprint","INTERSECT",VERTEX,{"derivedFrom":[subQ1,subQ0]});Q54=makeQuery(id+"F0.imprint","IMPRINT",FACE,{"disambiguationData":[TD([[makeQuery(id+"F0.imprint","IMPRINT",EDGE,{"disambiguationData":[TD([[subQ2,-1.0]])],"derivedFrom":subQ1}),-1.0]])]});}
            var Q55;
            {var subQ0=sQuery(id+"F0.wireOp",EDGE,"E16.0");var subQ1=sQuery(id+"F0.wireOp",EDGE,"E6.0");var subQ2=makeQuery(id+"F0.imprint","INTERSECT",VERTEX,{"derivedFrom":[subQ1,subQ0]});Q55=makeQuery(id+"F0.imprint","IMPRINT",FACE,{"disambiguationData":[TD([[makeQuery(id+"F0.imprint","IMPRINT",EDGE,{"disambiguationData":[TD([[subQ2,-1.0]])],"derivedFrom":subQ1}),-1.0]])]});}
            var Q56;
            {var subQ0=sQuery(id+"F0.wireOp",EDGE,"E13.0");var subQ1=sQuery(id+"F0.wireOp",EDGE,"E7.0");var subQ2=makeQuery(id+"F0.imprint","INTERSECT",VERTEX,{"derivedFrom":[subQ1,subQ0]});Q56=makeQuery(id+"F0.imprint","IMPRINT",FACE,{"disambiguationData":[TD([[makeQuery(id+"F0.imprint","IMPRINT",EDGE,{"disambiguationData":[TD([[subQ2,-1.0]])],"derivedFrom":subQ1}),-1.0]])]});}
            var Q57;
            {var subQ0=sQuery(id+"F0.wireOp",EDGE,"E11.0");var subQ1=sQuery(id+"F0.wireOp",EDGE,"E5.0");var subQ2=makeQuery(id+"F0.imprint","INTERSECT",VERTEX,{"derivedFrom":[subQ1,subQ0]});Q57=makeQuery(id+"F0.imprint","IMPRINT",FACE,{"disambiguationData":[TD([[makeQuery(id+"F0.imprint","IMPRINT",EDGE,{"disambiguationData":[TD([[subQ2,-1.0]])],"derivedFrom":subQ1}),-1.0]])]});}
            var Q58;
            {var subQ0=sQuery(id+"F0.wireOp",EDGE,"E16.0");var subQ1=sQuery(id+"F0.wireOp",EDGE,"E2.0");var subQ2=makeQuery(id+"F0.imprint","INTERSECT",VERTEX,{"derivedFrom":[subQ1,subQ0]});Q58=makeQuery(id+"F0.imprint","IMPRINT",FACE,{"disambiguationData":[TD([[makeQuery(id+"F0.imprint","IMPRINT",EDGE,{"disambiguationData":[TD([[subQ2,-1.0]])],"derivedFrom":subQ1}),-1.0]])]});}
            var Q59;
            {var subQ0=sQuery(id+"F0.wireOp",EDGE,"E14.0");var subQ1=sQuery(id+"F0.wireOp",EDGE,"E7.0");var subQ2=makeQuery(id+"F0.imprint","INTERSECT",VERTEX,{"derivedFrom":[subQ1,subQ0]});Q59=makeQuery(id+"F0.imprint","IMPRINT",FACE,{"disambiguationData":[TD([[makeQuery(id+"F0.imprint","IMPRINT",EDGE,{"disambiguationData":[TD([[subQ2,-1.0]])],"derivedFrom":subQ1}),-1.0]])]});}
            var Q60;
            {var subQ0=sQuery(id+"F0.wireOp",EDGE,"E12.0");var subQ1=sQuery(id+"F0.wireOp",EDGE,"E5.0");var subQ2=makeQuery(id+"F0.imprint","INTERSECT",VERTEX,{"derivedFrom":[subQ1,subQ0]});Q60=makeQuery(id+"F0.imprint","IMPRINT",FACE,{"disambiguationData":[TD([[makeQuery(id+"F0.imprint","IMPRINT",EDGE,{"disambiguationData":[TD([[subQ2,-1.0]])],"derivedFrom":subQ1}),-1.0]])]});}
            var Q61;
            {var subQ0=sQuery(id+"F0.wireOp",EDGE,"E17.0");var subQ1=sQuery(id+"F0.wireOp",EDGE,"E2.0");var subQ2=makeQuery(id+"F0.imprint","INTERSECT",VERTEX,{"derivedFrom":[subQ1,subQ0]});Q61=makeQuery(id+"F0.imprint","IMPRINT",FACE,{"disambiguationData":[TD([[makeQuery(id+"F0.imprint","IMPRINT",EDGE,{"disambiguationData":[TD([[subQ2,-1.0]])],"derivedFrom":subQ1}),-1.0]])]});}
            var Q62;
            {var subQ0=sQuery(id+"F0.wireOp",EDGE,"E16.0");var subQ1=sQuery(id+"F0.wireOp",EDGE,"E9.0");var subQ2=makeQuery(id+"F0.imprint","INTERSECT",VERTEX,{"derivedFrom":[subQ1,subQ0]});Q62=makeQuery(id+"F0.imprint","IMPRINT",FACE,{"disambiguationData":[TD([[makeQuery(id+"F0.imprint","IMPRINT",EDGE,{"disambiguationData":[TD([[subQ2,-1.0]])],"derivedFrom":subQ1}),-1.0]])]});}
            var Q63;
            {var subQ0=sQuery(id+"F0.wireOp",EDGE,"E13.0");var subQ1=sQuery(id+"F0.wireOp",EDGE,"E5.0");var subQ2=makeQuery(id+"F0.imprint","INTERSECT",VERTEX,{"derivedFrom":[subQ1,subQ0]});Q63=makeQuery(id+"F0.imprint","IMPRINT",FACE,{"disambiguationData":[TD([[makeQuery(id+"F0.imprint","IMPRINT",EDGE,{"disambiguationData":[TD([[subQ2,-1.0]])],"derivedFrom":subQ1}),-1.0]])]});}
            var Q64;
            {var subQ0=sQuery(id+"F0.wireOp",EDGE,"E11.0");var subQ1=sQuery(id+"F0.wireOp",EDGE,"E3.0");var subQ2=makeQuery(id+"F0.imprint","INTERSECT",VERTEX,{"derivedFrom":[subQ1,subQ0]});Q64=makeQuery(id+"F0.imprint","IMPRINT",FACE,{"disambiguationData":[TD([[makeQuery(id+"F0.imprint","IMPRINT",EDGE,{"disambiguationData":[TD([[subQ2,-1.0]])],"derivedFrom":subQ1}),-1.0]])]});}
            var Q65;
            {var subQ0=sQuery(id+"F0.wireOp",EDGE,"E17.0");var subQ1=sQuery(id+"F0.wireOp",EDGE,"E9.0");var subQ2=makeQuery(id+"F0.imprint","INTERSECT",VERTEX,{"derivedFrom":[subQ1,subQ0]});Q65=makeQuery(id+"F0.imprint","IMPRINT",FACE,{"disambiguationData":[TD([[makeQuery(id+"F0.imprint","IMPRINT",EDGE,{"disambiguationData":[TD([[subQ2,-1.0]])],"derivedFrom":subQ1}),-1.0]])]});}
            var Q66;
            {var subQ0=sQuery(id+"F0.wireOp",EDGE,"E16.0");var subQ1=sQuery(id+"F0.wireOp",EDGE,"E7.0");var subQ2=makeQuery(id+"F0.imprint","INTERSECT",VERTEX,{"derivedFrom":[subQ1,subQ0]});Q66=makeQuery(id+"F0.imprint","IMPRINT",FACE,{"disambiguationData":[TD([[makeQuery(id+"F0.imprint","IMPRINT",EDGE,{"disambiguationData":[TD([[subQ2,-1.0]])],"derivedFrom":subQ1}),-1.0]])]});}
            var Q67;
            {var subQ0=sQuery(id+"F0.wireOp",EDGE,"E14.0");var subQ1=sQuery(id+"F0.wireOp",EDGE,"E5.0");var subQ2=makeQuery(id+"F0.imprint","INTERSECT",VERTEX,{"derivedFrom":[subQ1,subQ0]});Q67=makeQuery(id+"F0.imprint","IMPRINT",FACE,{"disambiguationData":[TD([[makeQuery(id+"F0.imprint","IMPRINT",EDGE,{"disambiguationData":[TD([[subQ2,-1.0]])],"derivedFrom":subQ1}),-1.0]])]});}
            var Q68;
            {var subQ0=sQuery(id+"F0.wireOp",EDGE,"E12.0");var subQ1=sQuery(id+"F0.wireOp",EDGE,"E3.0");var subQ2=makeQuery(id+"F0.imprint","INTERSECT",VERTEX,{"derivedFrom":[subQ1,subQ0]});Q68=makeQuery(id+"F0.imprint","IMPRINT",FACE,{"disambiguationData":[TD([[makeQuery(id+"F0.imprint","IMPRINT",EDGE,{"disambiguationData":[TD([[subQ2,-1.0]])],"derivedFrom":subQ1}),-1.0]])]});}
            var Q69;
            {var subQ0=sQuery(id+"F0.wireOp",EDGE,"E17.0");var subQ1=sQuery(id+"F0.wireOp",EDGE,"E7.0");var subQ2=makeQuery(id+"F0.imprint","INTERSECT",VERTEX,{"derivedFrom":[subQ1,subQ0]});Q69=makeQuery(id+"F0.imprint","IMPRINT",FACE,{"disambiguationData":[TD([[makeQuery(id+"F0.imprint","IMPRINT",EDGE,{"disambiguationData":[TD([[subQ2,-1.0]])],"derivedFrom":subQ1}),-1.0]])]});}
            var Q70;
            {var subQ0=sQuery(id+"F0.wireOp",EDGE,"E13.0");var subQ1=sQuery(id+"F0.wireOp",EDGE,"E3.0");var subQ2=makeQuery(id+"F0.imprint","INTERSECT",VERTEX,{"derivedFrom":[subQ1,subQ0]});Q70=makeQuery(id+"F0.imprint","IMPRINT",FACE,{"disambiguationData":[TD([[makeQuery(id+"F0.imprint","IMPRINT",EDGE,{"disambiguationData":[TD([[subQ2,-1.0]])],"derivedFrom":subQ1}),-1.0]])]});}
            var Q71;
            {var subQ0=sQuery(id+"F0.wireOp",EDGE,"E11.0");var subQ1=sQuery(id+"F0.wireOp",EDGE,"E1.0");var subQ2=makeQuery(id+"F0.imprint","INTERSECT",VERTEX,{"derivedFrom":[subQ1,subQ0]});Q71=makeQuery(id+"F0.imprint","IMPRINT",FACE,{"disambiguationData":[TD([[makeQuery(id+"F0.imprint","IMPRINT",EDGE,{"disambiguationData":[TD([[subQ2,-1.0]])],"derivedFrom":subQ1}),-1.0]])]});}
            var Q72;
            {var subQ0=sQuery(id+"F0.wireOp",EDGE,"E11.0");var subQ1=sQuery(id+"F0.wireOp",EDGE,"E8.0");var subQ2=makeQuery(id+"F0.imprint","INTERSECT",VERTEX,{"derivedFrom":[subQ1,subQ0]});Q72=makeQuery(id+"F0.imprint","IMPRINT",FACE,{"disambiguationData":[TD([[makeQuery(id+"F0.imprint","IMPRINT",EDGE,{"disambiguationData":[TD([[subQ2,-1.0]])],"derivedFrom":subQ1}),-1.0]])]});}
            var Q73;
            {var subQ0=sQuery(id+"F0.wireOp",EDGE,"E16.0");var subQ1=sQuery(id+"F0.wireOp",EDGE,"E5.0");var subQ2=makeQuery(id+"F0.imprint","INTERSECT",VERTEX,{"derivedFrom":[subQ1,subQ0]});Q73=makeQuery(id+"F0.imprint","IMPRINT",FACE,{"disambiguationData":[TD([[makeQuery(id+"F0.imprint","IMPRINT",EDGE,{"disambiguationData":[TD([[subQ2,-1.0]])],"derivedFrom":subQ1}),-1.0]])]});}
            var Q74;
            {var subQ0=sQuery(id+"F0.wireOp",EDGE,"E14.0");var subQ1=sQuery(id+"F0.wireOp",EDGE,"E3.0");var subQ2=makeQuery(id+"F0.imprint","INTERSECT",VERTEX,{"derivedFrom":[subQ1,subQ0]});Q74=makeQuery(id+"F0.imprint","IMPRINT",FACE,{"disambiguationData":[TD([[makeQuery(id+"F0.imprint","IMPRINT",EDGE,{"disambiguationData":[TD([[subQ2,-1.0]])],"derivedFrom":subQ1}),-1.0]])]});}
            var Q75;
            {var subQ0=sQuery(id+"F0.wireOp",EDGE,"E12.0");var subQ1=sQuery(id+"F0.wireOp",EDGE,"E1.0");var subQ2=makeQuery(id+"F0.imprint","INTERSECT",VERTEX,{"derivedFrom":[subQ1,subQ0]});Q75=makeQuery(id+"F0.imprint","IMPRINT",FACE,{"disambiguationData":[TD([[makeQuery(id+"F0.imprint","IMPRINT",EDGE,{"disambiguationData":[TD([[subQ2,-1.0]])],"derivedFrom":subQ1}),-1.0]])]});}
            var Q76;
            {var subQ0=sQuery(id+"F0.wireOp",EDGE,"E17.0");var subQ1=sQuery(id+"F0.wireOp",EDGE,"E5.0");var subQ2=makeQuery(id+"F0.imprint","INTERSECT",VERTEX,{"derivedFrom":[subQ1,subQ0]});Q76=makeQuery(id+"F0.imprint","IMPRINT",FACE,{"disambiguationData":[TD([[makeQuery(id+"F0.imprint","IMPRINT",EDGE,{"disambiguationData":[TD([[subQ2,-1.0]])],"derivedFrom":subQ1}),-1.0]])]});}
            var Q77;
            {var subQ0=sQuery(id+"F0.wireOp",EDGE,"E15.0");var subQ1=sQuery(id+"F0.wireOp",EDGE,"E3.0");var subQ2=makeQuery(id+"F0.imprint","INTERSECT",VERTEX,{"derivedFrom":[subQ1,subQ0]});Q77=makeQuery(id+"F0.imprint","IMPRINT",FACE,{"disambiguationData":[TD([[makeQuery(id+"F0.imprint","IMPRINT",EDGE,{"disambiguationData":[TD([[subQ2,-1.0]])],"derivedFrom":subQ1}),-1.0]])]});}
            var Q78;
            {var subQ0=sQuery(id+"F0.wireOp",EDGE,"E13.0");var subQ1=sQuery(id+"F0.wireOp",EDGE,"E1.0");var subQ2=makeQuery(id+"F0.imprint","INTERSECT",VERTEX,{"derivedFrom":[subQ1,subQ0]});Q78=makeQuery(id+"F0.imprint","IMPRINT",FACE,{"disambiguationData":[TD([[makeQuery(id+"F0.imprint","IMPRINT",EDGE,{"disambiguationData":[TD([[subQ2,-1.0]])],"derivedFrom":subQ1}),-1.0]])]});}
            var Q79;
            {var subQ0=sQuery(id+"F0.wireOp",EDGE,"E16.0");var subQ1=sQuery(id+"F0.wireOp",EDGE,"E3.0");var subQ2=makeQuery(id+"F0.imprint","INTERSECT",VERTEX,{"derivedFrom":[subQ1,subQ0]});Q79=makeQuery(id+"F0.imprint","IMPRINT",FACE,{"disambiguationData":[TD([[makeQuery(id+"F0.imprint","IMPRINT",EDGE,{"disambiguationData":[TD([[subQ2,-1.0]])],"derivedFrom":subQ1}),-1.0]])]});}
            var Q80;
            {var subQ0=sQuery(id+"F0.wireOp",EDGE,"E14.0");var subQ1=sQuery(id+"F0.wireOp",EDGE,"E1.0");var subQ2=makeQuery(id+"F0.imprint","INTERSECT",VERTEX,{"derivedFrom":[subQ1,subQ0]});Q80=makeQuery(id+"F0.imprint","IMPRINT",FACE,{"disambiguationData":[TD([[makeQuery(id+"F0.imprint","IMPRINT",EDGE,{"disambiguationData":[TD([[subQ2,-1.0]])],"derivedFrom":subQ1}),-1.0]])]});}
            var Q81;
            {var subQ0=sQuery(id+"F0.wireOp",EDGE,"E13.0");var subQ1=sQuery(id+"F0.wireOp",EDGE,"E8.0");var subQ2=makeQuery(id+"F0.imprint","INTERSECT",VERTEX,{"derivedFrom":[subQ1,subQ0]});Q81=makeQuery(id+"F0.imprint","IMPRINT",FACE,{"disambiguationData":[TD([[makeQuery(id+"F0.imprint","IMPRINT",EDGE,{"disambiguationData":[TD([[subQ2,-1.0]])],"derivedFrom":subQ1}),-1.0]])]});}
            var Q82;
            {var subQ0=sQuery(id+"F0.wireOp",EDGE,"E11.0");var subQ1=sQuery(id+"F0.wireOp",EDGE,"E6.0");var subQ2=makeQuery(id+"F0.imprint","INTERSECT",VERTEX,{"derivedFrom":[subQ1,subQ0]});Q82=makeQuery(id+"F0.imprint","IMPRINT",FACE,{"disambiguationData":[TD([[makeQuery(id+"F0.imprint","IMPRINT",EDGE,{"disambiguationData":[TD([[subQ2,-1.0]])],"derivedFrom":subQ1}),-1.0]])]});}
            var Q83;
            {var subQ0=sQuery(id+"F0.wireOp",EDGE,"E17.0");var subQ1=sQuery(id+"F0.wireOp",EDGE,"E3.0");var subQ2=makeQuery(id+"F0.imprint","INTERSECT",VERTEX,{"derivedFrom":[subQ1,subQ0]});Q83=makeQuery(id+"F0.imprint","IMPRINT",FACE,{"disambiguationData":[TD([[makeQuery(id+"F0.imprint","IMPRINT",EDGE,{"disambiguationData":[TD([[subQ2,-1.0]])],"derivedFrom":subQ1}),-1.0]])]});}
            var Q84;
            {var subQ0=sQuery(id+"F0.wireOp",EDGE,"E15.0");var subQ1=sQuery(id+"F0.wireOp",EDGE,"E1.0");var subQ2=makeQuery(id+"F0.imprint","INTERSECT",VERTEX,{"derivedFrom":[subQ1,subQ0]});Q84=makeQuery(id+"F0.imprint","IMPRINT",FACE,{"disambiguationData":[TD([[makeQuery(id+"F0.imprint","IMPRINT",EDGE,{"disambiguationData":[TD([[subQ2,-1.0]])],"derivedFrom":subQ1}),-1.0]])]});}
            var Q85;
            {var subQ0=sQuery(id+"F0.wireOp",EDGE,"E14.0");var subQ1=sQuery(id+"F0.wireOp",EDGE,"E8.0");var subQ2=makeQuery(id+"F0.imprint","INTERSECT",VERTEX,{"derivedFrom":[subQ1,subQ0]});Q85=makeQuery(id+"F0.imprint","IMPRINT",FACE,{"disambiguationData":[TD([[makeQuery(id+"F0.imprint","IMPRINT",EDGE,{"disambiguationData":[TD([[subQ2,-1.0]])],"derivedFrom":subQ1}),-1.0]])]});}
            var Q86;
            {var subQ0=sQuery(id+"F0.wireOp",EDGE,"E11.0");var subQ1=sQuery(id+"F0.wireOp",EDGE,"E4.0");var subQ2=makeQuery(id+"F0.imprint","INTERSECT",VERTEX,{"derivedFrom":[subQ1,subQ0]});Q86=makeQuery(id+"F0.imprint","IMPRINT",FACE,{"disambiguationData":[TD([[makeQuery(id+"F0.imprint","IMPRINT",EDGE,{"disambiguationData":[TD([[subQ2,-1.0]])],"derivedFrom":subQ1}),-1.0]])]});}
            var Q87;
            {var subQ0=sQuery(id+"F0.wireOp",EDGE,"E16.0");var subQ1=sQuery(id+"F0.wireOp",EDGE,"E1.0");var subQ2=makeQuery(id+"F0.imprint","INTERSECT",VERTEX,{"derivedFrom":[subQ1,subQ0]});Q87=makeQuery(id+"F0.imprint","IMPRINT",FACE,{"disambiguationData":[TD([[makeQuery(id+"F0.imprint","IMPRINT",EDGE,{"disambiguationData":[TD([[subQ2,-1.0]])],"derivedFrom":subQ1}),-1.0]])]});}
            var Q88;
            {var subQ0=sQuery(id+"F0.wireOp",EDGE,"E14.0");var subQ1=sQuery(id+"F0.wireOp",EDGE,"E9.0");var subQ2=makeQuery(id+"F0.imprint","INTERSECT",VERTEX,{"derivedFrom":[subQ1,subQ0]});Q88=makeQuery(id+"F0.imprint","IMPRINT",FACE,{"disambiguationData":[TD([[makeQuery(id+"F0.imprint","IMPRINT",EDGE,{"disambiguationData":[TD([[subQ2,-1.0]])],"derivedFrom":subQ1}),-1.0]])]});}
            var Q89;
            {var subQ0=sQuery(id+"F0.wireOp",EDGE,"E12.0");var subQ1=sQuery(id+"F0.wireOp",EDGE,"E7.0");var subQ2=makeQuery(id+"F0.imprint","INTERSECT",VERTEX,{"derivedFrom":[subQ1,subQ0]});Q89=makeQuery(id+"F0.imprint","IMPRINT",FACE,{"disambiguationData":[TD([[makeQuery(id+"F0.imprint","IMPRINT",EDGE,{"disambiguationData":[TD([[subQ2,-1.0]])],"derivedFrom":subQ1}),-1.0]])]});}
            var Q90;
            {var subQ0=sQuery(id+"F0.wireOp",EDGE,"E17.0");var subQ1=sQuery(id+"F0.wireOp",EDGE,"E4.0");var subQ2=makeQuery(id+"F0.imprint","INTERSECT",VERTEX,{"derivedFrom":[subQ1,subQ0]});Q90=makeQuery(id+"F0.imprint","IMPRINT",FACE,{"disambiguationData":[TD([[makeQuery(id+"F0.imprint","IMPRINT",EDGE,{"disambiguationData":[TD([[subQ2,-1.0]])],"derivedFrom":subQ1}),-1.0]])]});}
            var Q91;
            {var subQ0=sQuery(id+"F0.wireOp",EDGE,"E15.0");var subQ1=sQuery(id+"F0.wireOp",EDGE,"E2.0");var subQ2=makeQuery(id+"F0.imprint","INTERSECT",VERTEX,{"derivedFrom":[subQ1,subQ0]});Q91=makeQuery(id+"F0.imprint","IMPRINT",FACE,{"disambiguationData":[TD([[makeQuery(id+"F0.imprint","IMPRINT",EDGE,{"disambiguationData":[TD([[subQ2,-1.0]])],"derivedFrom":subQ1}),-1.0]])]});}
            var Q92;
            {var subQ0=sQuery(id+"F0.wireOp",EDGE,"E13.0");var subQ1=sQuery(id+"F0.wireOp",EDGE,"E6.0");var subQ2=makeQuery(id+"F0.imprint","INTERSECT",VERTEX,{"derivedFrom":[subQ1,subQ0]});Q92=makeQuery(id+"F0.imprint","IMPRINT",FACE,{"disambiguationData":[TD([[makeQuery(id+"F0.imprint","IMPRINT",EDGE,{"disambiguationData":[TD([[subQ2,-1.0]])],"derivedFrom":subQ1}),-1.0]])]});}
            var Q93;
            {var subQ0=sQuery(id+"F0.wireOp",EDGE,"E15.0");var subQ1=sQuery(id+"F0.wireOp",EDGE,"E4.0");var subQ2=makeQuery(id+"F0.imprint","INTERSECT",VERTEX,{"derivedFrom":[subQ1,subQ0]});Q93=makeQuery(id+"F0.imprint","IMPRINT",FACE,{"disambiguationData":[TD([[makeQuery(id+"F0.imprint","IMPRINT",EDGE,{"disambiguationData":[TD([[subQ2,-1.0]])],"derivedFrom":subQ1}),-1.0]])]});}
            var Q94;
            {var subQ0=sQuery(id+"F0.wireOp",EDGE,"E15.0");var subQ1=sQuery(id+"F0.wireOp",EDGE,"E6.0");var subQ2=makeQuery(id+"F0.imprint","INTERSECT",VERTEX,{"derivedFrom":[subQ1,subQ0]});Q94=makeQuery(id+"F0.imprint","IMPRINT",FACE,{"disambiguationData":[TD([[makeQuery(id+"F0.imprint","IMPRINT",EDGE,{"disambiguationData":[TD([[subQ2,-1.0]])],"derivedFrom":subQ1}),-1.0]])]});}
            var Q95;
            {var subQ0=sQuery(id+"F0.wireOp",EDGE,"E15.0");var subQ1=sQuery(id+"F0.wireOp",EDGE,"E9.0");var subQ2=makeQuery(id+"F0.imprint","INTERSECT",VERTEX,{"derivedFrom":[subQ1,subQ0]});Q95=makeQuery(id+"F0.imprint","IMPRINT",FACE,{"disambiguationData":[TD([[makeQuery(id+"F0.imprint","IMPRINT",EDGE,{"disambiguationData":[TD([[subQ2,-1.0]])],"derivedFrom":subQ1}),-1.0]])]});}
            var Q96;
            {var subQ0=sQuery(id+"F0.wireOp",EDGE,"E15.0");var subQ1=sQuery(id+"F0.wireOp",EDGE,"E7.0");var subQ2=makeQuery(id+"F0.imprint","INTERSECT",VERTEX,{"derivedFrom":[subQ1,subQ0]});Q96=makeQuery(id+"F0.imprint","IMPRINT",FACE,{"disambiguationData":[TD([[makeQuery(id+"F0.imprint","IMPRINT",EDGE,{"disambiguationData":[TD([[subQ2,-1.0]])],"derivedFrom":subQ1}),-1.0]])]});}
            var Q97;
            {var subQ0=sQuery(id+"F0.wireOp",EDGE,"E15.0");var subQ1=sQuery(id+"F0.wireOp",EDGE,"E5.0");var subQ2=makeQuery(id+"F0.imprint","INTERSECT",VERTEX,{"derivedFrom":[subQ1,subQ0]});Q97=makeQuery(id+"F0.imprint","IMPRINT",FACE,{"disambiguationData":[TD([[makeQuery(id+"F0.imprint","IMPRINT",EDGE,{"disambiguationData":[TD([[subQ2,-1.0]])],"derivedFrom":subQ1}),-1.0]])]});}
            var Q98;
            {var subQ0=sQuery(id+"F0.wireOp",EDGE,"E15.0");var subQ1=sQuery(id+"F0.wireOp",EDGE,"E8.0");var subQ2=makeQuery(id+"F0.imprint","INTERSECT",VERTEX,{"derivedFrom":[subQ1,subQ0]});Q98=makeQuery(id+"F0.imprint","IMPRINT",FACE,{"disambiguationData":[TD([[makeQuery(id+"F0.imprint","IMPRINT",EDGE,{"disambiguationData":[TD([[subQ2,-1.0]])],"derivedFrom":subQ1}),-1.0]])]});}
            extrude(context, id + "F21", {"entities" : qUnion([Q0, Q1, Q2, Q3, Q4, Q5, Q6, Q7, Q8, Q9, Q10, Q11, Q12, Q13, Q14, Q15, Q16, Q17, Q18, Q19, Q20, Q21, Q22, Q23, Q24, Q25, Q26, Q27, Q28, Q29, Q30, Q31, Q32, Q33, Q34, Q35, Q36, Q37, Q38, Q39, Q40, Q41, Q42, Q43, Q44, Q45, Q46, Q47, Q48, Q49, Q50, Q51, Q52, Q53, Q54, Q55, Q56, Q57, Q58, Q59, Q60, Q61, Q62, Q63, Q64, Q65, Q66, Q67, Q68, Q69, Q70, Q71, Q72, Q73, Q74, Q75, Q76, Q77, Q78, Q79, Q80, Q81, Q82, Q83, Q84, Q85, Q86, Q87, Q88, Q89, Q90, Q91, Q92, Q93, Q94, Q95, Q96, Q97, Q98]), "operationType" : NewBodyOperationType.ADD, "oppositeDirection" : true, "depth" : 45 * mm, "offsetDistance" : 25 * mm});
        }
        {
            var Q0;
            {var subQ0=sQuery(id+"F0.wireOp",EDGE,"E11.0");var subQ1=sQuery(id+"F0.wireOp",EDGE,"E1.0");var subQ2=makeQuery(id+"F0.imprint","INTERSECT",VERTEX,{"derivedFrom":[subQ1,subQ0]});Q0=makeQuery(id+"F0.imprint","IMPRINT",FACE,{"disambiguationData":[TD([[makeQuery(id+"F0.imprint","IMPRINT",EDGE,{"disambiguationData":[TD([[subQ2,-1.0]])],"derivedFrom":subQ1}),-1.0]])]});}
            var Q1;
            {var subQ0=sQuery(id+"F0.wireOp",EDGE,"E12.0");var subQ1=sQuery(id+"F0.wireOp",EDGE,"E1.0");var subQ2=makeQuery(id+"F0.imprint","INTERSECT",VERTEX,{"derivedFrom":[subQ1,subQ0]});Q1=makeQuery(id+"F0.imprint","IMPRINT",FACE,{"disambiguationData":[TD([[makeQuery(id+"F0.imprint","IMPRINT",EDGE,{"disambiguationData":[TD([[subQ2,-1.0]])],"derivedFrom":subQ1}),-1.0]])]});}
            var Q2;
            {var subQ0=sQuery(id+"F0.wireOp",EDGE,"E13.0");var subQ1=sQuery(id+"F0.wireOp",EDGE,"E1.0");var subQ2=makeQuery(id+"F0.imprint","INTERSECT",VERTEX,{"derivedFrom":[subQ1,subQ0]});Q2=makeQuery(id+"F0.imprint","IMPRINT",FACE,{"disambiguationData":[TD([[makeQuery(id+"F0.imprint","IMPRINT",EDGE,{"disambiguationData":[TD([[subQ2,-1.0]])],"derivedFrom":subQ1}),-1.0]])]});}
            var Q3;
            {var subQ0=sQuery(id+"F0.wireOp",EDGE,"E14.0");var subQ1=sQuery(id+"F0.wireOp",EDGE,"E1.0");var subQ2=makeQuery(id+"F0.imprint","INTERSECT",VERTEX,{"derivedFrom":[subQ1,subQ0]});Q3=makeQuery(id+"F0.imprint","IMPRINT",FACE,{"disambiguationData":[TD([[makeQuery(id+"F0.imprint","IMPRINT",EDGE,{"disambiguationData":[TD([[subQ2,-1.0]])],"derivedFrom":subQ1}),-1.0]])]});}
            var Q4;
            {var subQ0=sQuery(id+"F0.wireOp",EDGE,"E15.0");var subQ1=sQuery(id+"F0.wireOp",EDGE,"E1.0");var subQ2=makeQuery(id+"F0.imprint","INTERSECT",VERTEX,{"derivedFrom":[subQ1,subQ0]});Q4=makeQuery(id+"F0.imprint","IMPRINT",FACE,{"disambiguationData":[TD([[makeQuery(id+"F0.imprint","IMPRINT",EDGE,{"disambiguationData":[TD([[subQ2,-1.0]])],"derivedFrom":subQ1}),-1.0]])]});}
            var Q5;
            {var subQ0=sQuery(id+"F0.wireOp",EDGE,"E16.0");var subQ1=sQuery(id+"F0.wireOp",EDGE,"E1.0");var subQ2=makeQuery(id+"F0.imprint","INTERSECT",VERTEX,{"derivedFrom":[subQ1,subQ0]});Q5=makeQuery(id+"F0.imprint","IMPRINT",FACE,{"disambiguationData":[TD([[makeQuery(id+"F0.imprint","IMPRINT",EDGE,{"disambiguationData":[TD([[subQ2,-1.0]])],"derivedFrom":subQ1}),-1.0]])]});}
            var Q6;
            {var subQ0=sQuery(id+"F0.wireOp",EDGE,"E17.0");var subQ1=sQuery(id+"F0.wireOp",EDGE,"E3.0");var subQ2=makeQuery(id+"F0.imprint","INTERSECT",VERTEX,{"derivedFrom":[subQ1,subQ0]});Q6=makeQuery(id+"F0.imprint","IMPRINT",FACE,{"disambiguationData":[TD([[makeQuery(id+"F0.imprint","IMPRINT",EDGE,{"disambiguationData":[TD([[subQ2,-1.0]])],"derivedFrom":subQ1}),-1.0]])]});}
            var Q7;
            {var subQ0=sQuery(id+"F0.wireOp",EDGE,"E15.0");var subQ1=sQuery(id+"F0.wireOp",EDGE,"E3.0");var subQ2=makeQuery(id+"F0.imprint","INTERSECT",VERTEX,{"derivedFrom":[subQ1,subQ0]});Q7=makeQuery(id+"F0.imprint","IMPRINT",FACE,{"disambiguationData":[TD([[makeQuery(id+"F0.imprint","IMPRINT",EDGE,{"disambiguationData":[TD([[subQ2,-1.0]])],"derivedFrom":subQ1}),-1.0]])]});}
            var Q8;
            {var subQ0=sQuery(id+"F0.wireOp",EDGE,"E16.0");var subQ1=sQuery(id+"F0.wireOp",EDGE,"E3.0");var subQ2=makeQuery(id+"F0.imprint","INTERSECT",VERTEX,{"derivedFrom":[subQ1,subQ0]});Q8=makeQuery(id+"F0.imprint","IMPRINT",FACE,{"disambiguationData":[TD([[makeQuery(id+"F0.imprint","IMPRINT",EDGE,{"disambiguationData":[TD([[subQ2,-1.0]])],"derivedFrom":subQ1}),-1.0]])]});}
            var Q9;
            {var subQ0=sQuery(id+"F0.wireOp",EDGE,"E14.0");var subQ1=sQuery(id+"F0.wireOp",EDGE,"E3.0");var subQ2=makeQuery(id+"F0.imprint","INTERSECT",VERTEX,{"derivedFrom":[subQ1,subQ0]});Q9=makeQuery(id+"F0.imprint","IMPRINT",FACE,{"disambiguationData":[TD([[makeQuery(id+"F0.imprint","IMPRINT",EDGE,{"disambiguationData":[TD([[subQ2,-1.0]])],"derivedFrom":subQ1}),-1.0]])]});}
            var Q10;
            {var subQ0=sQuery(id+"F0.wireOp",EDGE,"E13.0");var subQ1=sQuery(id+"F0.wireOp",EDGE,"E3.0");var subQ2=makeQuery(id+"F0.imprint","INTERSECT",VERTEX,{"derivedFrom":[subQ1,subQ0]});Q10=makeQuery(id+"F0.imprint","IMPRINT",FACE,{"disambiguationData":[TD([[makeQuery(id+"F0.imprint","IMPRINT",EDGE,{"disambiguationData":[TD([[subQ2,-1.0]])],"derivedFrom":subQ1}),-1.0]])]});}
            var Q11;
            {var subQ0=sQuery(id+"F0.wireOp",EDGE,"E12.0");var subQ1=sQuery(id+"F0.wireOp",EDGE,"E3.0");var subQ2=makeQuery(id+"F0.imprint","INTERSECT",VERTEX,{"derivedFrom":[subQ1,subQ0]});Q11=makeQuery(id+"F0.imprint","IMPRINT",FACE,{"disambiguationData":[TD([[makeQuery(id+"F0.imprint","IMPRINT",EDGE,{"disambiguationData":[TD([[subQ2,-1.0]])],"derivedFrom":subQ1}),-1.0]])]});}
            var Q12;
            {var subQ0=sQuery(id+"F0.wireOp",EDGE,"E11.0");var subQ1=sQuery(id+"F0.wireOp",EDGE,"E3.0");var subQ2=makeQuery(id+"F0.imprint","INTERSECT",VERTEX,{"derivedFrom":[subQ1,subQ0]});Q12=makeQuery(id+"F0.imprint","IMPRINT",FACE,{"disambiguationData":[TD([[makeQuery(id+"F0.imprint","IMPRINT",EDGE,{"disambiguationData":[TD([[subQ2,-1.0]])],"derivedFrom":subQ1}),-1.0]])]});}
            var Q13;
            {var subQ0=sQuery(id+"F0.wireOp",EDGE,"E11.0");var subQ1=sQuery(id+"F0.wireOp",EDGE,"E2.0");var subQ2=makeQuery(id+"F0.imprint","INTERSECT",VERTEX,{"derivedFrom":[subQ1,subQ0]});Q13=makeQuery(id+"F0.imprint","IMPRINT",FACE,{"disambiguationData":[TD([[makeQuery(id+"F0.imprint","IMPRINT",EDGE,{"disambiguationData":[TD([[subQ2,-1.0]])],"derivedFrom":subQ1}),-1.0]])]});}
            var Q14;
            {var subQ0=sQuery(id+"F0.wireOp",EDGE,"E13.0");var subQ1=sQuery(id+"F0.wireOp",EDGE,"E2.0");var subQ2=makeQuery(id+"F0.imprint","INTERSECT",VERTEX,{"derivedFrom":[subQ1,subQ0]});Q14=makeQuery(id+"F0.imprint","IMPRINT",FACE,{"disambiguationData":[TD([[makeQuery(id+"F0.imprint","IMPRINT",EDGE,{"disambiguationData":[TD([[subQ2,-1.0]])],"derivedFrom":subQ1}),-1.0]])]});}
            var Q15;
            {var subQ0=sQuery(id+"F0.wireOp",EDGE,"E15.0");var subQ1=sQuery(id+"F0.wireOp",EDGE,"E2.0");var subQ2=makeQuery(id+"F0.imprint","INTERSECT",VERTEX,{"derivedFrom":[subQ1,subQ0]});Q15=makeQuery(id+"F0.imprint","IMPRINT",FACE,{"disambiguationData":[TD([[makeQuery(id+"F0.imprint","IMPRINT",EDGE,{"disambiguationData":[TD([[subQ2,-1.0]])],"derivedFrom":subQ1}),-1.0]])]});}
            var Q16;
            {var subQ0=sQuery(id+"F0.wireOp",EDGE,"E17.0");var subQ1=sQuery(id+"F0.wireOp",EDGE,"E2.0");var subQ2=makeQuery(id+"F0.imprint","INTERSECT",VERTEX,{"derivedFrom":[subQ1,subQ0]});Q16=makeQuery(id+"F0.imprint","IMPRINT",FACE,{"disambiguationData":[TD([[makeQuery(id+"F0.imprint","IMPRINT",EDGE,{"disambiguationData":[TD([[subQ2,-1.0]])],"derivedFrom":subQ1}),-1.0]])]});}
            var Q17;
            {var subQ0=sQuery(id+"F0.wireOp",EDGE,"E17.0");var subQ1=sQuery(id+"F0.wireOp",EDGE,"E1.0");var subQ2=makeQuery(id+"F0.imprint","INTERSECT",VERTEX,{"derivedFrom":[subQ1,subQ0]});Q17=makeQuery(id+"F0.imprint","IMPRINT",FACE,{"disambiguationData":[TD([[makeQuery(id+"F0.imprint","IMPRINT",EDGE,{"disambiguationData":[TD([[subQ2,-1.0]])],"derivedFrom":subQ1}),-1.0]])]});}
            var Q18;
            {var subQ0=sQuery(id+"F0.wireOp",EDGE,"E17.0");var subQ1=sQuery(id+"F0.wireOp",EDGE,"E4.0");var subQ2=makeQuery(id+"F0.imprint","INTERSECT",VERTEX,{"derivedFrom":[subQ1,subQ0]});Q18=makeQuery(id+"F0.imprint","IMPRINT",FACE,{"disambiguationData":[TD([[makeQuery(id+"F0.imprint","IMPRINT",EDGE,{"disambiguationData":[TD([[subQ2,-1.0]])],"derivedFrom":subQ1}),-1.0]])]});}
            var Q19;
            {var subQ0=sQuery(id+"F0.wireOp",EDGE,"E15.0");var subQ1=sQuery(id+"F0.wireOp",EDGE,"E4.0");var subQ2=makeQuery(id+"F0.imprint","INTERSECT",VERTEX,{"derivedFrom":[subQ1,subQ0]});Q19=makeQuery(id+"F0.imprint","IMPRINT",FACE,{"disambiguationData":[TD([[makeQuery(id+"F0.imprint","IMPRINT",EDGE,{"disambiguationData":[TD([[subQ2,-1.0]])],"derivedFrom":subQ1}),-1.0]])]});}
            var Q20;
            {var subQ0=sQuery(id+"F0.wireOp",EDGE,"E13.0");var subQ1=sQuery(id+"F0.wireOp",EDGE,"E4.0");var subQ2=makeQuery(id+"F0.imprint","INTERSECT",VERTEX,{"derivedFrom":[subQ1,subQ0]});Q20=makeQuery(id+"F0.imprint","IMPRINT",FACE,{"disambiguationData":[TD([[makeQuery(id+"F0.imprint","IMPRINT",EDGE,{"disambiguationData":[TD([[subQ2,-1.0]])],"derivedFrom":subQ1}),-1.0]])]});}
            var Q21;
            {var subQ0=sQuery(id+"F0.wireOp",EDGE,"E11.0");var subQ1=sQuery(id+"F0.wireOp",EDGE,"E4.0");var subQ2=makeQuery(id+"F0.imprint","INTERSECT",VERTEX,{"derivedFrom":[subQ1,subQ0]});Q21=makeQuery(id+"F0.imprint","IMPRINT",FACE,{"disambiguationData":[TD([[makeQuery(id+"F0.imprint","IMPRINT",EDGE,{"disambiguationData":[TD([[subQ2,-1.0]])],"derivedFrom":subQ1}),-1.0]])]});}
            var Q22;
            {var subQ0=sQuery(id+"F0.wireOp",EDGE,"E12.0");var subQ1=sQuery(id+"F0.wireOp",EDGE,"E5.0");var subQ2=makeQuery(id+"F0.imprint","INTERSECT",VERTEX,{"derivedFrom":[subQ1,subQ0]});Q22=makeQuery(id+"F0.imprint","IMPRINT",FACE,{"disambiguationData":[TD([[makeQuery(id+"F0.imprint","IMPRINT",EDGE,{"disambiguationData":[TD([[subQ2,-1.0]])],"derivedFrom":subQ1}),-1.0]])]});}
            var Q23;
            {var subQ0=sQuery(id+"F0.wireOp",EDGE,"E11.0");var subQ1=sQuery(id+"F0.wireOp",EDGE,"E5.0");var subQ2=makeQuery(id+"F0.imprint","INTERSECT",VERTEX,{"derivedFrom":[subQ1,subQ0]});Q23=makeQuery(id+"F0.imprint","IMPRINT",FACE,{"disambiguationData":[TD([[makeQuery(id+"F0.imprint","IMPRINT",EDGE,{"disambiguationData":[TD([[subQ2,-1.0]])],"derivedFrom":subQ1}),-1.0]])]});}
            var Q24;
            {var subQ0=sQuery(id+"F0.wireOp",EDGE,"E11.0");var subQ1=sQuery(id+"F0.wireOp",EDGE,"E6.0");var subQ2=makeQuery(id+"F0.imprint","INTERSECT",VERTEX,{"derivedFrom":[subQ1,subQ0]});Q24=makeQuery(id+"F0.imprint","IMPRINT",FACE,{"disambiguationData":[TD([[makeQuery(id+"F0.imprint","IMPRINT",EDGE,{"disambiguationData":[TD([[subQ2,-1.0]])],"derivedFrom":subQ1}),-1.0]])]});}
            var Q25;
            {var subQ0=sQuery(id+"F0.wireOp",EDGE,"E11.0");var subQ1=sQuery(id+"F0.wireOp",EDGE,"E7.0");var subQ2=makeQuery(id+"F0.imprint","INTERSECT",VERTEX,{"derivedFrom":[subQ1,subQ0]});Q25=makeQuery(id+"F0.imprint","IMPRINT",FACE,{"disambiguationData":[TD([[makeQuery(id+"F0.imprint","IMPRINT",EDGE,{"disambiguationData":[TD([[subQ2,-1.0]])],"derivedFrom":subQ1}),-1.0]])]});}
            var Q26;
            {var subQ0=sQuery(id+"F0.wireOp",EDGE,"E11.0");var subQ1=sQuery(id+"F0.wireOp",EDGE,"E8.0");var subQ2=makeQuery(id+"F0.imprint","INTERSECT",VERTEX,{"derivedFrom":[subQ1,subQ0]});Q26=makeQuery(id+"F0.imprint","IMPRINT",FACE,{"disambiguationData":[TD([[makeQuery(id+"F0.imprint","IMPRINT",EDGE,{"disambiguationData":[TD([[subQ2,-1.0]])],"derivedFrom":subQ1}),-1.0]])]});}
            var Q27;
            {var subQ0=sQuery(id+"F0.wireOp",EDGE,"E11.0");var subQ1=sQuery(id+"F0.wireOp",EDGE,"E9.0");var subQ2=makeQuery(id+"F0.imprint","INTERSECT",VERTEX,{"derivedFrom":[subQ1,subQ0]});Q27=makeQuery(id+"F0.imprint","IMPRINT",FACE,{"disambiguationData":[TD([[makeQuery(id+"F0.imprint","IMPRINT",EDGE,{"disambiguationData":[TD([[subQ2,-1.0]])],"derivedFrom":subQ1}),-1.0]])]});}
            var Q28;
            {var subQ0=sQuery(id+"F0.wireOp",EDGE,"E12.0");var subQ1=sQuery(id+"F0.wireOp",EDGE,"E9.0");var subQ2=makeQuery(id+"F0.imprint","INTERSECT",VERTEX,{"derivedFrom":[subQ1,subQ0]});Q28=makeQuery(id+"F0.imprint","IMPRINT",FACE,{"disambiguationData":[TD([[makeQuery(id+"F0.imprint","IMPRINT",EDGE,{"disambiguationData":[TD([[subQ2,-1.0]])],"derivedFrom":subQ1}),-1.0]])]});}
            var Q29;
            {var subQ0=sQuery(id+"F0.wireOp",EDGE,"E13.0");var subQ1=sQuery(id+"F0.wireOp",EDGE,"E5.0");var subQ2=makeQuery(id+"F0.imprint","INTERSECT",VERTEX,{"derivedFrom":[subQ1,subQ0]});Q29=makeQuery(id+"F0.imprint","IMPRINT",FACE,{"disambiguationData":[TD([[makeQuery(id+"F0.imprint","IMPRINT",EDGE,{"disambiguationData":[TD([[subQ2,-1.0]])],"derivedFrom":subQ1}),-1.0]])]});}
            var Q30;
            {var subQ0=sQuery(id+"F0.wireOp",EDGE,"E13.0");var subQ1=sQuery(id+"F0.wireOp",EDGE,"E6.0");var subQ2=makeQuery(id+"F0.imprint","INTERSECT",VERTEX,{"derivedFrom":[subQ1,subQ0]});Q30=makeQuery(id+"F0.imprint","IMPRINT",FACE,{"disambiguationData":[TD([[makeQuery(id+"F0.imprint","IMPRINT",EDGE,{"disambiguationData":[TD([[subQ2,-1.0]])],"derivedFrom":subQ1}),-1.0]])]});}
            var Q31;
            {var subQ0=sQuery(id+"F0.wireOp",EDGE,"E13.0");var subQ1=sQuery(id+"F0.wireOp",EDGE,"E7.0");var subQ2=makeQuery(id+"F0.imprint","INTERSECT",VERTEX,{"derivedFrom":[subQ1,subQ0]});Q31=makeQuery(id+"F0.imprint","IMPRINT",FACE,{"disambiguationData":[TD([[makeQuery(id+"F0.imprint","IMPRINT",EDGE,{"disambiguationData":[TD([[subQ2,-1.0]])],"derivedFrom":subQ1}),-1.0]])]});}
            var Q32;
            {var subQ0=sQuery(id+"F0.wireOp",EDGE,"E13.0");var subQ1=sQuery(id+"F0.wireOp",EDGE,"E9.0");var subQ2=makeQuery(id+"F0.imprint","INTERSECT",VERTEX,{"derivedFrom":[subQ1,subQ0]});Q32=makeQuery(id+"F0.imprint","IMPRINT",FACE,{"disambiguationData":[TD([[makeQuery(id+"F0.imprint","IMPRINT",EDGE,{"disambiguationData":[TD([[subQ2,-1.0]])],"derivedFrom":subQ1}),-1.0]])]});}
            var Q33;
            {var subQ0=sQuery(id+"F0.wireOp",EDGE,"E13.0");var subQ1=sQuery(id+"F0.wireOp",EDGE,"E8.0");var subQ2=makeQuery(id+"F0.imprint","INTERSECT",VERTEX,{"derivedFrom":[subQ1,subQ0]});Q33=makeQuery(id+"F0.imprint","IMPRINT",FACE,{"disambiguationData":[TD([[makeQuery(id+"F0.imprint","IMPRINT",EDGE,{"disambiguationData":[TD([[subQ2,-1.0]])],"derivedFrom":subQ1}),-1.0]])]});}
            var Q34;
            {var subQ0=sQuery(id+"F0.wireOp",EDGE,"E17.0");var subQ1=sQuery(id+"F0.wireOp",EDGE,"E5.0");var subQ2=makeQuery(id+"F0.imprint","INTERSECT",VERTEX,{"derivedFrom":[subQ1,subQ0]});Q34=makeQuery(id+"F0.imprint","IMPRINT",FACE,{"disambiguationData":[TD([[makeQuery(id+"F0.imprint","IMPRINT",EDGE,{"disambiguationData":[TD([[subQ2,-1.0]])],"derivedFrom":subQ1}),-1.0]])]});}
            var Q35;
            {var subQ0=sQuery(id+"F0.wireOp",EDGE,"E16.0");var subQ1=sQuery(id+"F0.wireOp",EDGE,"E5.0");var subQ2=makeQuery(id+"F0.imprint","INTERSECT",VERTEX,{"derivedFrom":[subQ1,subQ0]});Q35=makeQuery(id+"F0.imprint","IMPRINT",FACE,{"disambiguationData":[TD([[makeQuery(id+"F0.imprint","IMPRINT",EDGE,{"disambiguationData":[TD([[subQ2,-1.0]])],"derivedFrom":subQ1}),-1.0]])]});}
            var Q36;
            {var subQ0=sQuery(id+"F0.wireOp",EDGE,"E15.0");var subQ1=sQuery(id+"F0.wireOp",EDGE,"E5.0");var subQ2=makeQuery(id+"F0.imprint","INTERSECT",VERTEX,{"derivedFrom":[subQ1,subQ0]});Q36=makeQuery(id+"F0.imprint","IMPRINT",FACE,{"disambiguationData":[TD([[makeQuery(id+"F0.imprint","IMPRINT",EDGE,{"disambiguationData":[TD([[subQ2,-1.0]])],"derivedFrom":subQ1}),-1.0]])]});}
            var Q37;
            {var subQ0=sQuery(id+"F0.wireOp",EDGE,"E14.0");var subQ1=sQuery(id+"F0.wireOp",EDGE,"E5.0");var subQ2=makeQuery(id+"F0.imprint","INTERSECT",VERTEX,{"derivedFrom":[subQ1,subQ0]});Q37=makeQuery(id+"F0.imprint","IMPRINT",FACE,{"disambiguationData":[TD([[makeQuery(id+"F0.imprint","IMPRINT",EDGE,{"disambiguationData":[TD([[subQ2,-1.0]])],"derivedFrom":subQ1}),-1.0]])]});}
            var Q38;
            {var subQ0=sQuery(id+"F0.wireOp",EDGE,"E15.0");var subQ1=sQuery(id+"F0.wireOp",EDGE,"E6.0");var subQ2=makeQuery(id+"F0.imprint","INTERSECT",VERTEX,{"derivedFrom":[subQ1,subQ0]});Q38=makeQuery(id+"F0.imprint","IMPRINT",FACE,{"disambiguationData":[TD([[makeQuery(id+"F0.imprint","IMPRINT",EDGE,{"disambiguationData":[TD([[subQ2,-1.0]])],"derivedFrom":subQ1}),-1.0]])]});}
            var Q39;
            {var subQ0=sQuery(id+"F0.wireOp",EDGE,"E17.0");var subQ1=sQuery(id+"F0.wireOp",EDGE,"E6.0");var subQ2=makeQuery(id+"F0.imprint","INTERSECT",VERTEX,{"derivedFrom":[subQ1,subQ0]});Q39=makeQuery(id+"F0.imprint","IMPRINT",FACE,{"disambiguationData":[TD([[makeQuery(id+"F0.imprint","IMPRINT",EDGE,{"disambiguationData":[TD([[subQ2,-1.0]])],"derivedFrom":subQ1}),-1.0]])]});}
            var Q40;
            {var subQ0=sQuery(id+"F0.wireOp",EDGE,"E14.0");var subQ1=sQuery(id+"F0.wireOp",EDGE,"E9.0");var subQ2=makeQuery(id+"F0.imprint","INTERSECT",VERTEX,{"derivedFrom":[subQ1,subQ0]});Q40=makeQuery(id+"F0.imprint","IMPRINT",FACE,{"disambiguationData":[TD([[makeQuery(id+"F0.imprint","IMPRINT",EDGE,{"disambiguationData":[TD([[subQ2,-1.0]])],"derivedFrom":subQ1}),-1.0]])]});}
            var Q41;
            {var subQ0=sQuery(id+"F0.wireOp",EDGE,"E14.0");var subQ1=sQuery(id+"F0.wireOp",EDGE,"E7.0");var subQ2=makeQuery(id+"F0.imprint","INTERSECT",VERTEX,{"derivedFrom":[subQ1,subQ0]});Q41=makeQuery(id+"F0.imprint","IMPRINT",FACE,{"disambiguationData":[TD([[makeQuery(id+"F0.imprint","IMPRINT",EDGE,{"disambiguationData":[TD([[subQ2,-1.0]])],"derivedFrom":subQ1}),-1.0]])]});}
            var Q42;
            {var subQ0=sQuery(id+"F0.wireOp",EDGE,"E15.0");var subQ1=sQuery(id+"F0.wireOp",EDGE,"E7.0");var subQ2=makeQuery(id+"F0.imprint","INTERSECT",VERTEX,{"derivedFrom":[subQ1,subQ0]});Q42=makeQuery(id+"F0.imprint","IMPRINT",FACE,{"disambiguationData":[TD([[makeQuery(id+"F0.imprint","IMPRINT",EDGE,{"disambiguationData":[TD([[subQ2,-1.0]])],"derivedFrom":subQ1}),-1.0]])]});}
            var Q43;
            {var subQ0=sQuery(id+"F0.wireOp",EDGE,"E16.0");var subQ1=sQuery(id+"F0.wireOp",EDGE,"E7.0");var subQ2=makeQuery(id+"F0.imprint","INTERSECT",VERTEX,{"derivedFrom":[subQ1,subQ0]});Q43=makeQuery(id+"F0.imprint","IMPRINT",FACE,{"disambiguationData":[TD([[makeQuery(id+"F0.imprint","IMPRINT",EDGE,{"disambiguationData":[TD([[subQ2,-1.0]])],"derivedFrom":subQ1}),-1.0]])]});}
            var Q44;
            {var subQ0=sQuery(id+"F0.wireOp",EDGE,"E16.0");var subQ1=sQuery(id+"F0.wireOp",EDGE,"E9.0");var subQ2=makeQuery(id+"F0.imprint","INTERSECT",VERTEX,{"derivedFrom":[subQ1,subQ0]});Q44=makeQuery(id+"F0.imprint","IMPRINT",FACE,{"disambiguationData":[TD([[makeQuery(id+"F0.imprint","IMPRINT",EDGE,{"disambiguationData":[TD([[subQ2,-1.0]])],"derivedFrom":subQ1}),-1.0]])]});}
            var Q45;
            {var subQ0=sQuery(id+"F0.wireOp",EDGE,"E17.0");var subQ1=sQuery(id+"F0.wireOp",EDGE,"E7.0");var subQ2=makeQuery(id+"F0.imprint","INTERSECT",VERTEX,{"derivedFrom":[subQ1,subQ0]});Q45=makeQuery(id+"F0.imprint","IMPRINT",FACE,{"disambiguationData":[TD([[makeQuery(id+"F0.imprint","IMPRINT",EDGE,{"disambiguationData":[TD([[subQ2,-1.0]])],"derivedFrom":subQ1}),-1.0]])]});}
            var Q46;
            {var subQ0=sQuery(id+"F0.wireOp",EDGE,"E17.0");var subQ1=sQuery(id+"F0.wireOp",EDGE,"E8.0");var subQ2=makeQuery(id+"F0.imprint","INTERSECT",VERTEX,{"derivedFrom":[subQ1,subQ0]});Q46=makeQuery(id+"F0.imprint","IMPRINT",FACE,{"disambiguationData":[TD([[makeQuery(id+"F0.imprint","IMPRINT",EDGE,{"disambiguationData":[TD([[subQ2,-1.0]])],"derivedFrom":subQ1}),-1.0]])]});}
            var Q47;
            {var subQ0=sQuery(id+"F0.wireOp",EDGE,"E17.0");var subQ1=sQuery(id+"F0.wireOp",EDGE,"E9.0");var subQ2=makeQuery(id+"F0.imprint","INTERSECT",VERTEX,{"derivedFrom":[subQ1,subQ0]});Q47=makeQuery(id+"F0.imprint","IMPRINT",FACE,{"disambiguationData":[TD([[makeQuery(id+"F0.imprint","IMPRINT",EDGE,{"disambiguationData":[TD([[subQ2,-1.0]])],"derivedFrom":subQ1}),-1.0]])]});}
            var Q48;
            {var subQ0=sQuery(id+"F0.wireOp",EDGE,"E15.0");var subQ1=sQuery(id+"F0.wireOp",EDGE,"E8.0");var subQ2=makeQuery(id+"F0.imprint","INTERSECT",VERTEX,{"derivedFrom":[subQ1,subQ0]});Q48=makeQuery(id+"F0.imprint","IMPRINT",FACE,{"disambiguationData":[TD([[makeQuery(id+"F0.imprint","IMPRINT",EDGE,{"disambiguationData":[TD([[subQ2,-1.0]])],"derivedFrom":subQ1}),-1.0]])]});}
            var Q49;
            {var subQ0=sQuery(id+"F0.wireOp",EDGE,"E15.0");var subQ1=sQuery(id+"F0.wireOp",EDGE,"E9.0");var subQ2=makeQuery(id+"F0.imprint","INTERSECT",VERTEX,{"derivedFrom":[subQ1,subQ0]});Q49=makeQuery(id+"F0.imprint","IMPRINT",FACE,{"disambiguationData":[TD([[makeQuery(id+"F0.imprint","IMPRINT",EDGE,{"disambiguationData":[TD([[subQ2,-1.0]])],"derivedFrom":subQ1}),-1.0]])]});}
            var Q50;
            {var subQ0=sQuery(id+"F0.wireOp",EDGE,"E12.0");var subQ1=sQuery(id+"F0.wireOp",EDGE,"E7.0");var subQ2=makeQuery(id+"F0.imprint","INTERSECT",VERTEX,{"derivedFrom":[subQ1,subQ0]});Q50=makeQuery(id+"F0.imprint","IMPRINT",FACE,{"disambiguationData":[TD([[makeQuery(id+"F0.imprint","IMPRINT",EDGE,{"disambiguationData":[TD([[subQ2,-1.0]])],"derivedFrom":subQ1}),-1.0]])]});}
            extrude(context, id + "F22", {"entities" : qUnion([Q0, Q1, Q2, Q3, Q4, Q5, Q6, Q7, Q8, Q9, Q10, Q11, Q12, Q13, Q14, Q15, Q16, Q17, Q18, Q19, Q20, Q21, Q22, Q23, Q24, Q25, Q26, Q27, Q28, Q29, Q30, Q31, Q32, Q33, Q34, Q35, Q36, Q37, Q38, Q39, Q40, Q41, Q42, Q43, Q44, Q45, Q46, Q47, Q48, Q49, Q50]), "oppositeDirection" : true, "depth" : 10 * mm, "offsetDistance" : 25 * mm});
        }
        {
            var Q0;
            Q0=makeQuery(id+"F22.opExtrude","SWEPT_BODY",BODY,{"disambiguationData":[OSD([sQuery(id+"F0.wireOp",EDGE,"E1.0"),sQuery(id+"F0.wireOp",EDGE,"E2.0"),sQuery(id+"F0.wireOp",EDGE,"E3.0"),sQuery(id+"F0.wireOp",EDGE,"E4.0"),sQuery(id+"F0.wireOp",EDGE,"E5.0"),sQuery(id+"F0.wireOp",EDGE,"E6.0"),sQuery(id+"F0.wireOp",EDGE,"E7.0"),sQuery(id+"F0.wireOp",EDGE,"E8.0"),sQuery(id+"F0.wireOp",EDGE,"E9.0"),sQuery(id+"F0.wireOp",EDGE,"E10.0"),sQuery(id+"F0.wireOp",EDGE,"E11.0"),sQuery(id+"F0.wireOp",EDGE,"E12.0"),sQuery(id+"F0.wireOp",EDGE,"E13.0"),sQuery(id+"F0.wireOp",EDGE,"E14.0"),sQuery(id+"F0.wireOp",EDGE,"E15.0"),sQuery(id+"F0.wireOp",EDGE,"E16.0"),sQuery(id+"F0.wireOp",EDGE,"E17.0"),sQuery(id+"F0.wireOp",EDGE,"E18.0")])]});
            var Q1;
            Q1=makeQuery(id+"F1.opExtrude","SWEPT_BODY",BODY,{"disambiguationData":[OSD([sQuery(id+"F0.wireOp",EDGE,"E0.top"),sQuery(id+"F0.wireOp",EDGE,"E0.right"),sQuery(id+"F0.wireOp",EDGE,"E1.0"),sQuery(id+"F0.wireOp",EDGE,"E18.0")])]});
            booleanBodies(context, id + "F23", {"operationType" : BooleanOperationType.SUBTRACTION, "tools" : qUnion([Q0]), "targets" : qUnion([Q1]), "keepTools" : true});
        }
        {
            var Q0;
            Q0=makeQuery(id+"F21.opExtrude","CAP_FACE",FACE,{"disambiguationData":[OSD([sQuery(id+"F0.wireOp",EDGE,"E0.bottom"),sQuery(id+"F0.wireOp",EDGE,"E0.top"),sQuery(id+"F0.wireOp",EDGE,"E0.left"),sQuery(id+"F0.wireOp",EDGE,"E0.right")])],"isStart":false});
            var sketch = newSketch(context, id + "F24", { "sketchPlane" : qUnion([Q0])});
            skLineSegment(sketch, "E19.bottom", {"start": v(95, 80) * mm, "end": v(-95, 80) * mm});
            skLineSegment(sketch, "E19.top", {"start": v(95, -80) * mm, "end": v(-95, -80) * mm});
            skLineSegment(sketch, "E19.left", {"start": v(95, 80) * mm, "end": v(95, -80) * mm});
            skLineSegment(sketch, "E19.right", {"start": v(-95, 80) * mm, "end": v(-95, -80) * mm});
            skPoint(sketch, "E19.middle", {"position": v(0, 0) * mm});
            skSolve(sketch);
        }
        {
            var Q0;
            Q0=makeQuery(id+"F24.imprint","IMPRINT",FACE,{"disambiguationData":[TD([[makeQuery(id+"F24.imprint","IMPRINT",EDGE,{"derivedFrom":sQuery(id+"F24.wireOp",EDGE,"E19.bottom")}),1.0]])]});
            var Q1;
            Q1=makeQuery(id+"F22.opExtrude","CAP_FACE",FACE,{"disambiguationData":[OSD([sQuery(id+"F0.wireOp",EDGE,"E1.0"),sQuery(id+"F0.wireOp",EDGE,"E2.0"),sQuery(id+"F0.wireOp",EDGE,"E3.0"),sQuery(id+"F0.wireOp",EDGE,"E4.0"),sQuery(id+"F0.wireOp",EDGE,"E5.0"),sQuery(id+"F0.wireOp",EDGE,"E6.0"),sQuery(id+"F0.wireOp",EDGE,"E7.0"),sQuery(id+"F0.wireOp",EDGE,"E8.0"),sQuery(id+"F0.wireOp",EDGE,"E9.0"),sQuery(id+"F0.wireOp",EDGE,"E10.0"),sQuery(id+"F0.wireOp",EDGE,"E11.0"),sQuery(id+"F0.wireOp",EDGE,"E12.0"),sQuery(id+"F0.wireOp",EDGE,"E13.0"),sQuery(id+"F0.wireOp",EDGE,"E14.0"),sQuery(id+"F0.wireOp",EDGE,"E15.0"),sQuery(id+"F0.wireOp",EDGE,"E16.0"),sQuery(id+"F0.wireOp",EDGE,"E17.0"),sQuery(id+"F0.wireOp",EDGE,"E18.0")])],"isStart":false});
            extrude(context, id + "F25", {"entities" : qUnion([Q0]), "operationType" : NewBodyOperationType.REMOVE, "endBound" : BoundingType.UP_TO_SURFACE, "oppositeDirection" : true, "depth" : 25 * mm, "endBoundEntityFace" : qUnion([Q1]), "offsetDistance" : 25 * mm});
        }
    });
